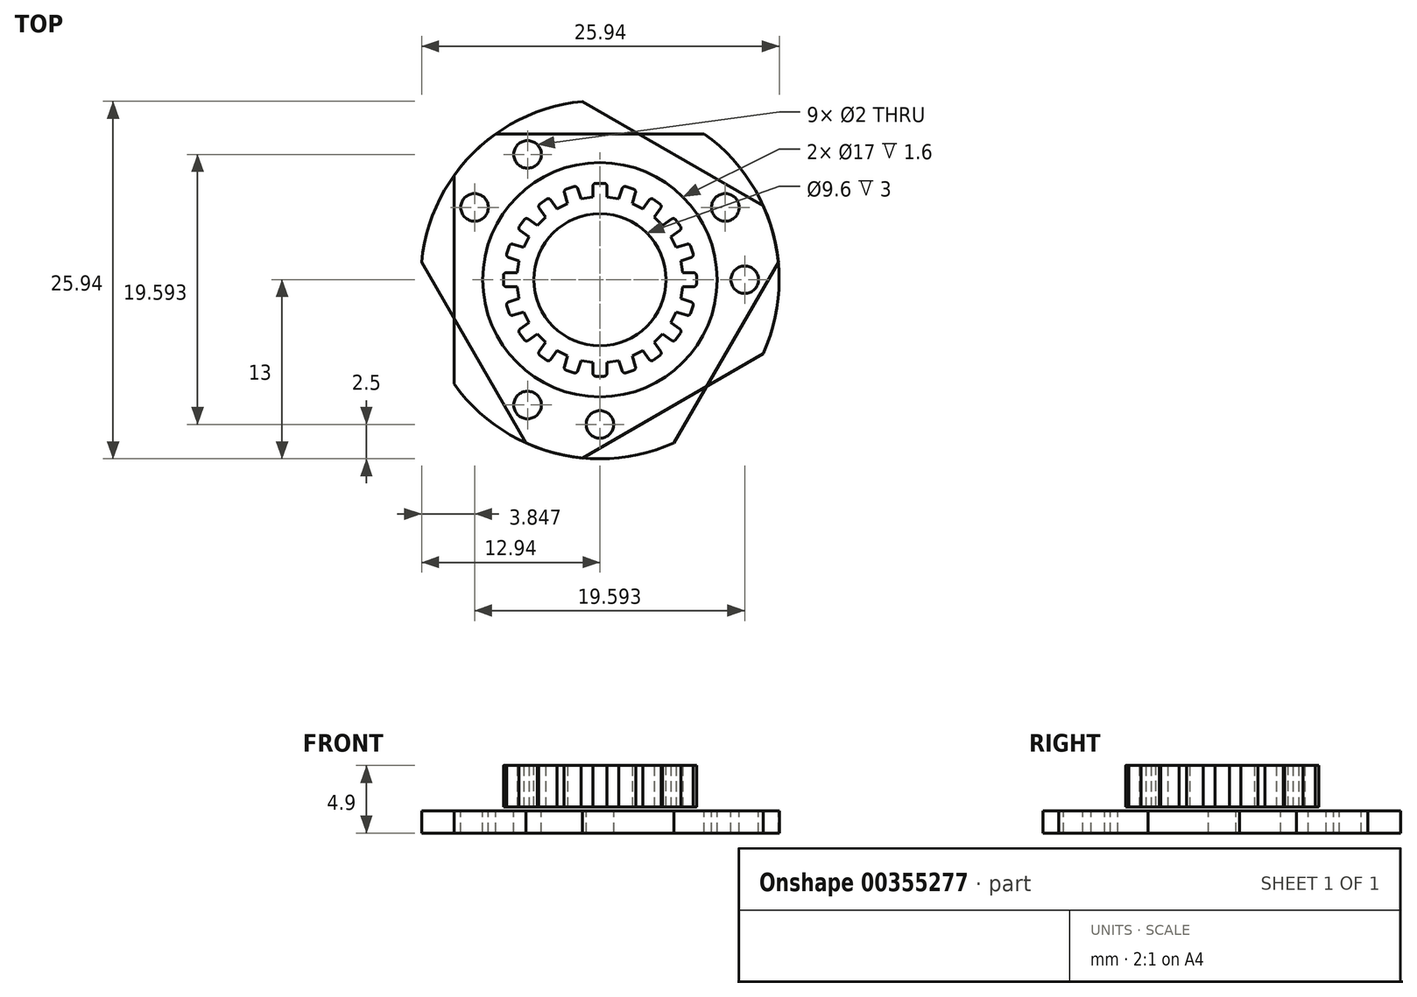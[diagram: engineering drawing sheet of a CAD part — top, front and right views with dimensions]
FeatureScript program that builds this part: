
annotation { "Feature Type Name" : "Feature", "Feature Type Description" : "" }
export const myFeature = defineFeature(function(context is Context, id is Id, definition is map)
    precondition{}
    {
        {
            assignVariable(context, id + "F0", {"name" : "THICK", "anyValue" : 3});
        }
        {
            var Q0;
            Q0=qCreatedBy(makeId("Top.planeOp"),FACE);
            var sketch = newSketch(context, id + "F1", { "sketchPlane" : qUnion([Q0])});
            skCircle(sketch, "E0", {"center": v(0, 0) * mm, "radius": 4 * mm});
            skCircle(sketch, "E1", {"center": v(0, 0) * mm, "radius": 3.5 * mm});
            skCircle(sketch, "E2", {"center": v(0, 0) * mm, "radius": 3 * mm});
            skSolve(sketch);
        }
        {
            var Q0;
            Q0=qCreatedBy(makeId("Top.planeOp"),FACE);
            var sketch = newSketch(context, id + "F2", { "sketchPlane" : qUnion([Q0])});
            skLineSegment(sketch, "E3", {"start": v(0, 0) * mm, "end": v(0, 4.84) * mm, "construction": true});
            skLineSegment(sketch, "E4", {"start": v(1.8, 5.57) * mm, "end": v(0, 0) * mm, "construction": true});
            skLineSegment(sketch, "E5", {"start": v(0.85, 5.38) * mm, "end": v(0, 0) * mm, "construction": true});
            skLineSegment(sketch, "E6", {"start": v(0, 4) * mm, "end": v(0.37, 4) * mm});
            skLineSegment(sketch, "E7", {"start": v(0.52, 3.86) * mm, "end": v(0.58, 2.97) * mm});
            skLineSegment(sketch, "E8", {"start": v(0.58, 2.97) * mm, "end": v(0.93, 2.85) * mm});
            skPoint(sketch, "E9.visualSharp", {"position": v(0.51, 4) * mm});
            skArc(sketch, "E9.filletArc", {"start": v(0.52, 3.86) * mm, "mid": v(0.47, 3.96) * mm, "end": v(0.37, 4) * mm});
            skLineSegment(sketch, "E10.MirrorCS", {"start": v(1.27, 2.74) * mm, "end": v(0.93, 2.85) * mm});
            skLineSegment(sketch, "E11.MirrorCS", {"start": v(2.35, 3.24) * mm, "end": v(2.05, 3.45) * mm});
            skLineSegment(sketch, "E12.MirrorCS", {"start": v(1.85, 3.43) * mm, "end": v(1.27, 2.74) * mm});
            skArc(sketch, "E13.MirrorCS", {"start": v(1.85, 3.43) * mm, "mid": v(1.95, 3.48) * mm, "end": v(2.05, 3.45) * mm});
            skLineSegment(sketch, "E14.1.0", {"start": v(-2.35, 3.24) * mm, "end": v(-2.05, 3.45) * mm});
            skArc(sketch, "E14.1.1", {"start": v(-1.85, 3.43) * mm, "mid": v(-1.95, 3.48) * mm, "end": v(-2.05, 3.45) * mm});
            skLineSegment(sketch, "E14.1.2", {"start": v(-1.85, 3.43) * mm, "end": v(-1.27, 2.74) * mm});
            skLineSegment(sketch, "E14.1.3", {"start": v(-1.27, 2.74) * mm, "end": v(-0.93, 2.85) * mm});
            skLineSegment(sketch, "E14.1.4", {"start": v(-0.58, 2.97) * mm, "end": v(-0.93, 2.85) * mm});
            skLineSegment(sketch, "E14.1.5", {"start": v(-0.52, 3.86) * mm, "end": v(-0.58, 2.97) * mm});
            skLineSegment(sketch, "E14.1.6", {"start": v(0, 4) * mm, "end": v(-0.37, 4) * mm});
            skArc(sketch, "E14.1.7", {"start": v(-0.52, 3.86) * mm, "mid": v(-0.47, 3.96) * mm, "end": v(-0.37, 4) * mm});
            skLineSegment(sketch, "E14.2.0", {"start": v(-3.8, 1.24) * mm, "end": v(-3.69, 1.59) * mm});
            skArc(sketch, "E14.2.1", {"start": v(-3.51, 1.69) * mm, "mid": v(-3.62, 1.67) * mm, "end": v(-3.69, 1.59) * mm});
            skLineSegment(sketch, "E14.2.2", {"start": v(-3.51, 1.69) * mm, "end": v(-2.64, 1.47) * mm});
            skLineSegment(sketch, "E14.2.3", {"start": v(-2.64, 1.47) * mm, "end": v(-2.43, 1.76) * mm});
            skLineSegment(sketch, "E14.2.4", {"start": v(-2.21, 2.06) * mm, "end": v(-2.43, 1.76) * mm});
            skLineSegment(sketch, "E14.2.5", {"start": v(-2.69, 2.82) * mm, "end": v(-2.21, 2.06) * mm});
            skLineSegment(sketch, "E14.2.6", {"start": v(-2.35, 3.24) * mm, "end": v(-2.65, 3.02) * mm});
            skArc(sketch, "E14.2.7", {"start": v(-2.69, 2.82) * mm, "mid": v(-2.7, 2.93) * mm, "end": v(-2.65, 3.02) * mm});
            skLineSegment(sketch, "E14.3.0", {"start": v(-3.8, -1.24) * mm, "end": v(-3.92, -0.88) * mm});
            skArc(sketch, "E14.3.1", {"start": v(-3.83, -0.7) * mm, "mid": v(-3.91, -0.77) * mm, "end": v(-3.92, -0.88) * mm});
            skLineSegment(sketch, "E14.3.2", {"start": v(-3.83, -0.7) * mm, "end": v(-3, -0.37) * mm});
            skLineSegment(sketch, "E14.3.3", {"start": v(-3, -0.37) * mm, "end": v(-3, 0) * mm});
            skLineSegment(sketch, "E14.3.4", {"start": v(-3, 0.37) * mm, "end": v(-3, 0) * mm});
            skLineSegment(sketch, "E14.3.5", {"start": v(-3.83, 0.7) * mm, "end": v(-3, 0.37) * mm});
            skLineSegment(sketch, "E14.3.6", {"start": v(-3.8, 1.24) * mm, "end": v(-3.92, 0.88) * mm});
            skArc(sketch, "E14.3.7", {"start": v(-3.83, 0.7) * mm, "mid": v(-3.91, 0.77) * mm, "end": v(-3.92, 0.88) * mm});
            skLineSegment(sketch, "E14.4.0", {"start": v(-2.35, -3.24) * mm, "end": v(-2.65, -3.02) * mm});
            skArc(sketch, "E14.4.1", {"start": v(-2.69, -2.82) * mm, "mid": v(-2.7, -2.93) * mm, "end": v(-2.65, -3.02) * mm});
            skLineSegment(sketch, "E14.4.2", {"start": v(-2.69, -2.82) * mm, "end": v(-2.21, -2.06) * mm});
            skLineSegment(sketch, "E14.4.3", {"start": v(-2.21, -2.06) * mm, "end": v(-2.43, -1.76) * mm});
            skLineSegment(sketch, "E14.4.4", {"start": v(-2.64, -1.47) * mm, "end": v(-2.43, -1.76) * mm});
            skLineSegment(sketch, "E14.4.5", {"start": v(-3.51, -1.69) * mm, "end": v(-2.64, -1.47) * mm});
            skLineSegment(sketch, "E14.4.6", {"start": v(-3.8, -1.24) * mm, "end": v(-3.69, -1.59) * mm});
            skArc(sketch, "E14.4.7", {"start": v(-3.51, -1.69) * mm, "mid": v(-3.62, -1.67) * mm, "end": v(-3.69, -1.59) * mm});
            skLineSegment(sketch, "E14.5.0", {"start": v(0, -4) * mm, "end": v(-0.37, -4) * mm});
            skArc(sketch, "E14.5.1", {"start": v(-0.52, -3.86) * mm, "mid": v(-0.47, -3.96) * mm, "end": v(-0.37, -4) * mm});
            skLineSegment(sketch, "E14.5.2", {"start": v(-0.52, -3.86) * mm, "end": v(-0.58, -2.97) * mm});
            skLineSegment(sketch, "E14.5.3", {"start": v(-0.58, -2.97) * mm, "end": v(-0.93, -2.85) * mm});
            skLineSegment(sketch, "E14.5.4", {"start": v(-1.27, -2.74) * mm, "end": v(-0.93, -2.85) * mm});
            skLineSegment(sketch, "E14.5.5", {"start": v(-1.85, -3.43) * mm, "end": v(-1.27, -2.74) * mm});
            skLineSegment(sketch, "E14.5.6", {"start": v(-2.35, -3.24) * mm, "end": v(-2.05, -3.45) * mm});
            skArc(sketch, "E14.5.7", {"start": v(-1.85, -3.43) * mm, "mid": v(-1.95, -3.48) * mm, "end": v(-2.05, -3.45) * mm});
            skLineSegment(sketch, "E14.6.0", {"start": v(2.35, -3.24) * mm, "end": v(2.05, -3.45) * mm});
            skArc(sketch, "E14.6.1", {"start": v(1.85, -3.43) * mm, "mid": v(1.95, -3.48) * mm, "end": v(2.05, -3.45) * mm});
            skLineSegment(sketch, "E14.6.2", {"start": v(1.85, -3.43) * mm, "end": v(1.27, -2.74) * mm});
            skLineSegment(sketch, "E14.6.3", {"start": v(1.27, -2.74) * mm, "end": v(0.93, -2.85) * mm});
            skLineSegment(sketch, "E14.6.4", {"start": v(0.58, -2.97) * mm, "end": v(0.93, -2.85) * mm});
            skLineSegment(sketch, "E14.6.5", {"start": v(0.52, -3.86) * mm, "end": v(0.58, -2.97) * mm});
            skLineSegment(sketch, "E14.6.6", {"start": v(0, -4) * mm, "end": v(0.37, -4) * mm});
            skArc(sketch, "E14.6.7", {"start": v(0.52, -3.86) * mm, "mid": v(0.47, -3.96) * mm, "end": v(0.37, -4) * mm});
            skLineSegment(sketch, "E14.7.0", {"start": v(3.8, -1.24) * mm, "end": v(3.69, -1.59) * mm});
            skArc(sketch, "E14.7.1", {"start": v(3.51, -1.69) * mm, "mid": v(3.62, -1.67) * mm, "end": v(3.69, -1.59) * mm});
            skLineSegment(sketch, "E14.7.2", {"start": v(3.51, -1.69) * mm, "end": v(2.64, -1.47) * mm});
            skLineSegment(sketch, "E14.7.3", {"start": v(2.64, -1.47) * mm, "end": v(2.43, -1.76) * mm});
            skLineSegment(sketch, "E14.7.4", {"start": v(2.21, -2.06) * mm, "end": v(2.43, -1.76) * mm});
            skLineSegment(sketch, "E14.7.5", {"start": v(2.69, -2.82) * mm, "end": v(2.21, -2.06) * mm});
            skLineSegment(sketch, "E14.7.6", {"start": v(2.35, -3.24) * mm, "end": v(2.65, -3.02) * mm});
            skArc(sketch, "E14.7.7", {"start": v(2.69, -2.82) * mm, "mid": v(2.7, -2.93) * mm, "end": v(2.65, -3.02) * mm});
            skLineSegment(sketch, "E14.8.0", {"start": v(3.8, 1.24) * mm, "end": v(3.92, 0.88) * mm});
            skArc(sketch, "E14.8.1", {"start": v(3.83, 0.7) * mm, "mid": v(3.91, 0.77) * mm, "end": v(3.92, 0.88) * mm});
            skLineSegment(sketch, "E14.8.2", {"start": v(3.83, 0.7) * mm, "end": v(3, 0.37) * mm});
            skLineSegment(sketch, "E14.8.3", {"start": v(3, 0.37) * mm, "end": v(3, 0) * mm});
            skLineSegment(sketch, "E14.8.4", {"start": v(3, -0.37) * mm, "end": v(3, 0) * mm});
            skLineSegment(sketch, "E14.8.5", {"start": v(3.83, -0.7) * mm, "end": v(3, -0.37) * mm});
            skLineSegment(sketch, "E14.8.6", {"start": v(3.8, -1.24) * mm, "end": v(3.92, -0.88) * mm});
            skArc(sketch, "E14.8.7", {"start": v(3.83, -0.7) * mm, "mid": v(3.91, -0.77) * mm, "end": v(3.92, -0.88) * mm});
            skLineSegment(sketch, "E14.9.0", {"start": v(2.35, 3.24) * mm, "end": v(2.65, 3.02) * mm});
            skArc(sketch, "E14.9.1", {"start": v(2.69, 2.82) * mm, "mid": v(2.7, 2.93) * mm, "end": v(2.65, 3.02) * mm});
            skLineSegment(sketch, "E14.9.2", {"start": v(2.69, 2.82) * mm, "end": v(2.21, 2.06) * mm});
            skLineSegment(sketch, "E14.9.3", {"start": v(2.21, 2.06) * mm, "end": v(2.43, 1.76) * mm});
            skLineSegment(sketch, "E14.9.4", {"start": v(2.64, 1.47) * mm, "end": v(2.43, 1.76) * mm});
            skLineSegment(sketch, "E14.9.5", {"start": v(3.51, 1.69) * mm, "end": v(2.64, 1.47) * mm});
            skLineSegment(sketch, "E14.9.6", {"start": v(3.8, 1.24) * mm, "end": v(3.69, 1.59) * mm});
            skArc(sketch, "E14.9.7", {"start": v(3.51, 1.69) * mm, "mid": v(3.62, 1.67) * mm, "end": v(3.69, 1.59) * mm});
            skPoint(sketch, "E14.center", {"position": v(0, 0) * mm});
            skSolve(sketch);
        }
        {
            var Q0;
            Q0=qSketchRegion(id+"F2",true);
            extrude(context, id + "F3", {"entities" : qUnion([Q0]), "depth" : (getVariable(context, 'THICK')) * mm});
        }
        {
            var Q0;
            Q0=makeQuery(id+"F3.opExtrude","CAP_FACE",FACE,{"disambiguationData":[OSD([sQuery(id+"F2.wireOp",EDGE,"E6"),sQuery(id+"F2.wireOp",EDGE,"E7"),sQuery(id+"F2.wireOp",EDGE,"E8"),sQuery(id+"F2.wireOp",EDGE,"E9.filletArc"),sQuery(id+"F2.wireOp",EDGE,"E10.MirrorCS"),sQuery(id+"F2.wireOp",EDGE,"E11.MirrorCS"),sQuery(id+"F2.wireOp",EDGE,"E12.MirrorCS"),sQuery(id+"F2.wireOp",EDGE,"E13.MirrorCS"),sQuery(id+"F2.wireOp",EDGE,"E14.1.0"),sQuery(id+"F2.wireOp",EDGE,"E14.1.1"),sQuery(id+"F2.wireOp",EDGE,"E14.1.2"),sQuery(id+"F2.wireOp",EDGE,"E14.1.3"),sQuery(id+"F2.wireOp",EDGE,"E14.1.4"),sQuery(id+"F2.wireOp",EDGE,"E14.1.5"),sQuery(id+"F2.wireOp",EDGE,"E14.1.6"),sQuery(id+"F2.wireOp",EDGE,"E14.1.7"),sQuery(id+"F2.wireOp",EDGE,"E14.2.0"),sQuery(id+"F2.wireOp",EDGE,"E14.2.1"),sQuery(id+"F2.wireOp",EDGE,"E14.2.2"),sQuery(id+"F2.wireOp",EDGE,"E14.2.3"),sQuery(id+"F2.wireOp",EDGE,"E14.2.4"),sQuery(id+"F2.wireOp",EDGE,"E14.2.5"),sQuery(id+"F2.wireOp",EDGE,"E14.2.6"),sQuery(id+"F2.wireOp",EDGE,"E14.2.7"),sQuery(id+"F2.wireOp",EDGE,"E14.3.0"),sQuery(id+"F2.wireOp",EDGE,"E14.3.1"),sQuery(id+"F2.wireOp",EDGE,"E14.3.2"),sQuery(id+"F2.wireOp",EDGE,"E14.3.3"),sQuery(id+"F2.wireOp",EDGE,"E14.3.4"),sQuery(id+"F2.wireOp",EDGE,"E14.3.5"),sQuery(id+"F2.wireOp",EDGE,"E14.3.6"),sQuery(id+"F2.wireOp",EDGE,"E14.3.7"),sQuery(id+"F2.wireOp",EDGE,"E14.4.0"),sQuery(id+"F2.wireOp",EDGE,"E14.4.1"),sQuery(id+"F2.wireOp",EDGE,"E14.4.2"),sQuery(id+"F2.wireOp",EDGE,"E14.4.3"),sQuery(id+"F2.wireOp",EDGE,"E14.4.4"),sQuery(id+"F2.wireOp",EDGE,"E14.4.5"),sQuery(id+"F2.wireOp",EDGE,"E14.4.6"),sQuery(id+"F2.wireOp",EDGE,"E14.4.7"),sQuery(id+"F2.wireOp",EDGE,"E14.5.0"),sQuery(id+"F2.wireOp",EDGE,"E14.5.1"),sQuery(id+"F2.wireOp",EDGE,"E14.5.2"),sQuery(id+"F2.wireOp",EDGE,"E14.5.3"),sQuery(id+"F2.wireOp",EDGE,"E14.5.4"),sQuery(id+"F2.wireOp",EDGE,"E14.5.5"),sQuery(id+"F2.wireOp",EDGE,"E14.5.6"),sQuery(id+"F2.wireOp",EDGE,"E14.5.7"),sQuery(id+"F2.wireOp",EDGE,"E14.6.0"),sQuery(id+"F2.wireOp",EDGE,"E14.6.1"),sQuery(id+"F2.wireOp",EDGE,"E14.6.2"),sQuery(id+"F2.wireOp",EDGE,"E14.6.3"),sQuery(id+"F2.wireOp",EDGE,"E14.6.4"),sQuery(id+"F2.wireOp",EDGE,"E14.6.5"),sQuery(id+"F2.wireOp",EDGE,"E14.6.6"),sQuery(id+"F2.wireOp",EDGE,"E14.6.7"),sQuery(id+"F2.wireOp",EDGE,"E14.7.0"),sQuery(id+"F2.wireOp",EDGE,"E14.7.1"),sQuery(id+"F2.wireOp",EDGE,"E14.7.2"),sQuery(id+"F2.wireOp",EDGE,"E14.7.3"),sQuery(id+"F2.wireOp",EDGE,"E14.7.4"),sQuery(id+"F2.wireOp",EDGE,"E14.7.5"),sQuery(id+"F2.wireOp",EDGE,"E14.7.6"),sQuery(id+"F2.wireOp",EDGE,"E14.7.7"),sQuery(id+"F2.wireOp",EDGE,"E14.8.0"),sQuery(id+"F2.wireOp",EDGE,"E14.8.1"),sQuery(id+"F2.wireOp",EDGE,"E14.8.2"),sQuery(id+"F2.wireOp",EDGE,"E14.8.3"),sQuery(id+"F2.wireOp",EDGE,"E14.8.4"),sQuery(id+"F2.wireOp",EDGE,"E14.8.5"),sQuery(id+"F2.wireOp",EDGE,"E14.8.6"),sQuery(id+"F2.wireOp",EDGE,"E14.8.7"),sQuery(id+"F2.wireOp",EDGE,"E14.9.0"),sQuery(id+"F2.wireOp",EDGE,"E14.9.1"),sQuery(id+"F2.wireOp",EDGE,"E14.9.2"),sQuery(id+"F2.wireOp",EDGE,"E14.9.3"),sQuery(id+"F2.wireOp",EDGE,"E14.9.4"),sQuery(id+"F2.wireOp",EDGE,"E14.9.5"),sQuery(id+"F2.wireOp",EDGE,"E14.9.6"),sQuery(id+"F2.wireOp",EDGE,"E14.9.7")])],"isStart":true});
            var sketch = newSketch(context, id + "F4", { "sketchPlane" : qUnion([Q0])});
            skCircle(sketch, "E15", {"center": v(0, 0) * mm, "radius": 2.25 * mm});
            skSolve(sketch);
        }
        {
            var Q0;
            Q0=qSketchRegion(id+"F4",true);
            extrude(context, id + "F5", {"entities" : qUnion([Q0]), "operationType" : NewBodyOperationType.ADD, "depth" : 0.3 * mm});
        }
        {
            var Q0;
            Q0=makeQuery(id+"F3.opExtrude","SWEPT_BODY",BODY,{"disambiguationData":[OSD([sQuery(id+"F2.wireOp",EDGE,"E6"),sQuery(id+"F2.wireOp",EDGE,"E7"),sQuery(id+"F2.wireOp",EDGE,"E8"),sQuery(id+"F2.wireOp",EDGE,"E9.filletArc"),sQuery(id+"F2.wireOp",EDGE,"E10.MirrorCS"),sQuery(id+"F2.wireOp",EDGE,"E11.MirrorCS"),sQuery(id+"F2.wireOp",EDGE,"E12.MirrorCS"),sQuery(id+"F2.wireOp",EDGE,"E13.MirrorCS"),sQuery(id+"F2.wireOp",EDGE,"E14.1.0"),sQuery(id+"F2.wireOp",EDGE,"E14.1.1"),sQuery(id+"F2.wireOp",EDGE,"E14.1.2"),sQuery(id+"F2.wireOp",EDGE,"E14.1.3"),sQuery(id+"F2.wireOp",EDGE,"E14.1.4"),sQuery(id+"F2.wireOp",EDGE,"E14.1.5"),sQuery(id+"F2.wireOp",EDGE,"E14.1.6"),sQuery(id+"F2.wireOp",EDGE,"E14.1.7"),sQuery(id+"F2.wireOp",EDGE,"E14.2.0"),sQuery(id+"F2.wireOp",EDGE,"E14.2.1"),sQuery(id+"F2.wireOp",EDGE,"E14.2.2"),sQuery(id+"F2.wireOp",EDGE,"E14.2.3"),sQuery(id+"F2.wireOp",EDGE,"E14.2.4"),sQuery(id+"F2.wireOp",EDGE,"E14.2.5"),sQuery(id+"F2.wireOp",EDGE,"E14.2.6"),sQuery(id+"F2.wireOp",EDGE,"E14.2.7"),sQuery(id+"F2.wireOp",EDGE,"E14.3.0"),sQuery(id+"F2.wireOp",EDGE,"E14.3.1"),sQuery(id+"F2.wireOp",EDGE,"E14.3.2"),sQuery(id+"F2.wireOp",EDGE,"E14.3.3"),sQuery(id+"F2.wireOp",EDGE,"E14.3.4"),sQuery(id+"F2.wireOp",EDGE,"E14.3.5"),sQuery(id+"F2.wireOp",EDGE,"E14.3.6"),sQuery(id+"F2.wireOp",EDGE,"E14.3.7"),sQuery(id+"F2.wireOp",EDGE,"E14.4.0"),sQuery(id+"F2.wireOp",EDGE,"E14.4.1"),sQuery(id+"F2.wireOp",EDGE,"E14.4.2"),sQuery(id+"F2.wireOp",EDGE,"E14.4.3"),sQuery(id+"F2.wireOp",EDGE,"E14.4.4"),sQuery(id+"F2.wireOp",EDGE,"E14.4.5"),sQuery(id+"F2.wireOp",EDGE,"E14.4.6"),sQuery(id+"F2.wireOp",EDGE,"E14.4.7"),sQuery(id+"F2.wireOp",EDGE,"E14.5.0"),sQuery(id+"F2.wireOp",EDGE,"E14.5.1"),sQuery(id+"F2.wireOp",EDGE,"E14.5.2"),sQuery(id+"F2.wireOp",EDGE,"E14.5.3"),sQuery(id+"F2.wireOp",EDGE,"E14.5.4"),sQuery(id+"F2.wireOp",EDGE,"E14.5.5"),sQuery(id+"F2.wireOp",EDGE,"E14.5.6"),sQuery(id+"F2.wireOp",EDGE,"E14.5.7"),sQuery(id+"F2.wireOp",EDGE,"E14.6.0"),sQuery(id+"F2.wireOp",EDGE,"E14.6.1"),sQuery(id+"F2.wireOp",EDGE,"E14.6.2"),sQuery(id+"F2.wireOp",EDGE,"E14.6.3"),sQuery(id+"F2.wireOp",EDGE,"E14.6.4"),sQuery(id+"F2.wireOp",EDGE,"E14.6.5"),sQuery(id+"F2.wireOp",EDGE,"E14.6.6"),sQuery(id+"F2.wireOp",EDGE,"E14.6.7"),sQuery(id+"F2.wireOp",EDGE,"E14.7.0"),sQuery(id+"F2.wireOp",EDGE,"E14.7.1"),sQuery(id+"F2.wireOp",EDGE,"E14.7.2"),sQuery(id+"F2.wireOp",EDGE,"E14.7.3"),sQuery(id+"F2.wireOp",EDGE,"E14.7.4"),sQuery(id+"F2.wireOp",EDGE,"E14.7.5"),sQuery(id+"F2.wireOp",EDGE,"E14.7.6"),sQuery(id+"F2.wireOp",EDGE,"E14.7.7"),sQuery(id+"F2.wireOp",EDGE,"E14.8.0"),sQuery(id+"F2.wireOp",EDGE,"E14.8.1"),sQuery(id+"F2.wireOp",EDGE,"E14.8.2"),sQuery(id+"F2.wireOp",EDGE,"E14.8.3"),sQuery(id+"F2.wireOp",EDGE,"E14.8.4"),sQuery(id+"F2.wireOp",EDGE,"E14.8.5"),sQuery(id+"F2.wireOp",EDGE,"E14.8.6"),sQuery(id+"F2.wireOp",EDGE,"E14.8.7"),sQuery(id+"F2.wireOp",EDGE,"E14.9.0"),sQuery(id+"F2.wireOp",EDGE,"E14.9.1"),sQuery(id+"F2.wireOp",EDGE,"E14.9.2"),sQuery(id+"F2.wireOp",EDGE,"E14.9.3"),sQuery(id+"F2.wireOp",EDGE,"E14.9.4"),sQuery(id+"F2.wireOp",EDGE,"E14.9.5"),sQuery(id+"F2.wireOp",EDGE,"E14.9.6"),sQuery(id+"F2.wireOp",EDGE,"E14.9.7")])]});
            transform(context, id + "F6", {"entities" : qUnion([Q0]), "transformType" : TransformType.COPY});
        }
        {
            var Q0;
            Q0=makeQuery(id+"F3.opExtrude","CAP_FACE",FACE,{"disambiguationData":[OSD([sQuery(id+"F2.wireOp",EDGE,"E6"),sQuery(id+"F2.wireOp",EDGE,"E7"),sQuery(id+"F2.wireOp",EDGE,"E8"),sQuery(id+"F2.wireOp",EDGE,"E9.filletArc"),sQuery(id+"F2.wireOp",EDGE,"E10.MirrorCS"),sQuery(id+"F2.wireOp",EDGE,"E11.MirrorCS"),sQuery(id+"F2.wireOp",EDGE,"E12.MirrorCS"),sQuery(id+"F2.wireOp",EDGE,"E13.MirrorCS"),sQuery(id+"F2.wireOp",EDGE,"E14.1.0"),sQuery(id+"F2.wireOp",EDGE,"E14.1.1"),sQuery(id+"F2.wireOp",EDGE,"E14.1.2"),sQuery(id+"F2.wireOp",EDGE,"E14.1.3"),sQuery(id+"F2.wireOp",EDGE,"E14.1.4"),sQuery(id+"F2.wireOp",EDGE,"E14.1.5"),sQuery(id+"F2.wireOp",EDGE,"E14.1.6"),sQuery(id+"F2.wireOp",EDGE,"E14.1.7"),sQuery(id+"F2.wireOp",EDGE,"E14.2.0"),sQuery(id+"F2.wireOp",EDGE,"E14.2.1"),sQuery(id+"F2.wireOp",EDGE,"E14.2.2"),sQuery(id+"F2.wireOp",EDGE,"E14.2.3"),sQuery(id+"F2.wireOp",EDGE,"E14.2.4"),sQuery(id+"F2.wireOp",EDGE,"E14.2.5"),sQuery(id+"F2.wireOp",EDGE,"E14.2.6"),sQuery(id+"F2.wireOp",EDGE,"E14.2.7"),sQuery(id+"F2.wireOp",EDGE,"E14.3.0"),sQuery(id+"F2.wireOp",EDGE,"E14.3.1"),sQuery(id+"F2.wireOp",EDGE,"E14.3.2"),sQuery(id+"F2.wireOp",EDGE,"E14.3.3"),sQuery(id+"F2.wireOp",EDGE,"E14.3.4"),sQuery(id+"F2.wireOp",EDGE,"E14.3.5"),sQuery(id+"F2.wireOp",EDGE,"E14.3.6"),sQuery(id+"F2.wireOp",EDGE,"E14.3.7"),sQuery(id+"F2.wireOp",EDGE,"E14.4.0"),sQuery(id+"F2.wireOp",EDGE,"E14.4.1"),sQuery(id+"F2.wireOp",EDGE,"E14.4.2"),sQuery(id+"F2.wireOp",EDGE,"E14.4.3"),sQuery(id+"F2.wireOp",EDGE,"E14.4.4"),sQuery(id+"F2.wireOp",EDGE,"E14.4.5"),sQuery(id+"F2.wireOp",EDGE,"E14.4.6"),sQuery(id+"F2.wireOp",EDGE,"E14.4.7"),sQuery(id+"F2.wireOp",EDGE,"E14.5.0"),sQuery(id+"F2.wireOp",EDGE,"E14.5.1"),sQuery(id+"F2.wireOp",EDGE,"E14.5.2"),sQuery(id+"F2.wireOp",EDGE,"E14.5.3"),sQuery(id+"F2.wireOp",EDGE,"E14.5.4"),sQuery(id+"F2.wireOp",EDGE,"E14.5.5"),sQuery(id+"F2.wireOp",EDGE,"E14.5.6"),sQuery(id+"F2.wireOp",EDGE,"E14.5.7"),sQuery(id+"F2.wireOp",EDGE,"E14.6.0"),sQuery(id+"F2.wireOp",EDGE,"E14.6.1"),sQuery(id+"F2.wireOp",EDGE,"E14.6.2"),sQuery(id+"F2.wireOp",EDGE,"E14.6.3"),sQuery(id+"F2.wireOp",EDGE,"E14.6.4"),sQuery(id+"F2.wireOp",EDGE,"E14.6.5"),sQuery(id+"F2.wireOp",EDGE,"E14.6.6"),sQuery(id+"F2.wireOp",EDGE,"E14.6.7"),sQuery(id+"F2.wireOp",EDGE,"E14.7.0"),sQuery(id+"F2.wireOp",EDGE,"E14.7.1"),sQuery(id+"F2.wireOp",EDGE,"E14.7.2"),sQuery(id+"F2.wireOp",EDGE,"E14.7.3"),sQuery(id+"F2.wireOp",EDGE,"E14.7.4"),sQuery(id+"F2.wireOp",EDGE,"E14.7.5"),sQuery(id+"F2.wireOp",EDGE,"E14.7.6"),sQuery(id+"F2.wireOp",EDGE,"E14.7.7"),sQuery(id+"F2.wireOp",EDGE,"E14.8.0"),sQuery(id+"F2.wireOp",EDGE,"E14.8.1"),sQuery(id+"F2.wireOp",EDGE,"E14.8.2"),sQuery(id+"F2.wireOp",EDGE,"E14.8.3"),sQuery(id+"F2.wireOp",EDGE,"E14.8.4"),sQuery(id+"F2.wireOp",EDGE,"E14.8.5"),sQuery(id+"F2.wireOp",EDGE,"E14.8.6"),sQuery(id+"F2.wireOp",EDGE,"E14.8.7"),sQuery(id+"F2.wireOp",EDGE,"E14.9.0"),sQuery(id+"F2.wireOp",EDGE,"E14.9.1"),sQuery(id+"F2.wireOp",EDGE,"E14.9.2"),sQuery(id+"F2.wireOp",EDGE,"E14.9.3"),sQuery(id+"F2.wireOp",EDGE,"E14.9.4"),sQuery(id+"F2.wireOp",EDGE,"E14.9.5"),sQuery(id+"F2.wireOp",EDGE,"E14.9.6"),sQuery(id+"F2.wireOp",EDGE,"E14.9.7")])],"isStart":false});
            var sketch = newSketch(context, id + "F7", { "sketchPlane" : qUnion([Q0])});
            skCircle(sketch, "E16.cCircle", {"center": v(0, 0) * mm, "radius": 0.86 * mm, "construction": true});
            skLineSegment(sketch, "E16.0", {"start": v(0.86, 0.5) * mm, "end": v(0.86, -0.5) * mm});
            skLineSegment(sketch, "E16.1", {"start": v(0.86, -0.5) * mm, "end": v(0, -1) * mm});
            skLineSegment(sketch, "E16.2", {"start": v(0, -1) * mm, "end": v(-0.86, -0.5) * mm});
            skLineSegment(sketch, "E16.3", {"start": v(-0.86, -0.5) * mm, "end": v(-0.86, 0.5) * mm});
            skLineSegment(sketch, "E16.4", {"start": v(-0.86, 0.5) * mm, "end": v(0, 1) * mm});
            skLineSegment(sketch, "E16.5", {"start": v(0, 1) * mm, "end": v(0.86, 0.5) * mm});
            skPoint(sketch, "E16.0.midPoint", {"position": v(0.86, 0) * mm});
            skSolve(sketch);
        }
        {
            var Q0;
            Q0=qSketchRegion(id+"F7",true);
            extrude(context, id + "F8", {"entities" : qUnion([Q0]), "operationType" : NewBodyOperationType.REMOVE, "oppositeDirection" : true, "depth" : 25 * mm});
        }
        {
            var Q0;
            Q0=makeQuery(id+"F3.opExtrude","CAP_FACE",FACE,{"disambiguationData":[OSD([sQuery(id+"F2.wireOp",EDGE,"E6"),sQuery(id+"F2.wireOp",EDGE,"E7"),sQuery(id+"F2.wireOp",EDGE,"E8"),sQuery(id+"F2.wireOp",EDGE,"E9.filletArc"),sQuery(id+"F2.wireOp",EDGE,"E10.MirrorCS"),sQuery(id+"F2.wireOp",EDGE,"E11.MirrorCS"),sQuery(id+"F2.wireOp",EDGE,"E12.MirrorCS"),sQuery(id+"F2.wireOp",EDGE,"E13.MirrorCS"),sQuery(id+"F2.wireOp",EDGE,"E14.1.0"),sQuery(id+"F2.wireOp",EDGE,"E14.1.1"),sQuery(id+"F2.wireOp",EDGE,"E14.1.2"),sQuery(id+"F2.wireOp",EDGE,"E14.1.3"),sQuery(id+"F2.wireOp",EDGE,"E14.1.4"),sQuery(id+"F2.wireOp",EDGE,"E14.1.5"),sQuery(id+"F2.wireOp",EDGE,"E14.1.6"),sQuery(id+"F2.wireOp",EDGE,"E14.1.7"),sQuery(id+"F2.wireOp",EDGE,"E14.2.0"),sQuery(id+"F2.wireOp",EDGE,"E14.2.1"),sQuery(id+"F2.wireOp",EDGE,"E14.2.2"),sQuery(id+"F2.wireOp",EDGE,"E14.2.3"),sQuery(id+"F2.wireOp",EDGE,"E14.2.4"),sQuery(id+"F2.wireOp",EDGE,"E14.2.5"),sQuery(id+"F2.wireOp",EDGE,"E14.2.6"),sQuery(id+"F2.wireOp",EDGE,"E14.2.7"),sQuery(id+"F2.wireOp",EDGE,"E14.3.0"),sQuery(id+"F2.wireOp",EDGE,"E14.3.1"),sQuery(id+"F2.wireOp",EDGE,"E14.3.2"),sQuery(id+"F2.wireOp",EDGE,"E14.3.3"),sQuery(id+"F2.wireOp",EDGE,"E14.3.4"),sQuery(id+"F2.wireOp",EDGE,"E14.3.5"),sQuery(id+"F2.wireOp",EDGE,"E14.3.6"),sQuery(id+"F2.wireOp",EDGE,"E14.3.7"),sQuery(id+"F2.wireOp",EDGE,"E14.4.0"),sQuery(id+"F2.wireOp",EDGE,"E14.4.1"),sQuery(id+"F2.wireOp",EDGE,"E14.4.2"),sQuery(id+"F2.wireOp",EDGE,"E14.4.3"),sQuery(id+"F2.wireOp",EDGE,"E14.4.4"),sQuery(id+"F2.wireOp",EDGE,"E14.4.5"),sQuery(id+"F2.wireOp",EDGE,"E14.4.6"),sQuery(id+"F2.wireOp",EDGE,"E14.4.7"),sQuery(id+"F2.wireOp",EDGE,"E14.5.0"),sQuery(id+"F2.wireOp",EDGE,"E14.5.1"),sQuery(id+"F2.wireOp",EDGE,"E14.5.2"),sQuery(id+"F2.wireOp",EDGE,"E14.5.3"),sQuery(id+"F2.wireOp",EDGE,"E14.5.4"),sQuery(id+"F2.wireOp",EDGE,"E14.5.5"),sQuery(id+"F2.wireOp",EDGE,"E14.5.6"),sQuery(id+"F2.wireOp",EDGE,"E14.5.7"),sQuery(id+"F2.wireOp",EDGE,"E14.6.0"),sQuery(id+"F2.wireOp",EDGE,"E14.6.1"),sQuery(id+"F2.wireOp",EDGE,"E14.6.2"),sQuery(id+"F2.wireOp",EDGE,"E14.6.3"),sQuery(id+"F2.wireOp",EDGE,"E14.6.4"),sQuery(id+"F2.wireOp",EDGE,"E14.6.5"),sQuery(id+"F2.wireOp",EDGE,"E14.6.6"),sQuery(id+"F2.wireOp",EDGE,"E14.6.7"),sQuery(id+"F2.wireOp",EDGE,"E14.7.0"),sQuery(id+"F2.wireOp",EDGE,"E14.7.1"),sQuery(id+"F2.wireOp",EDGE,"E14.7.2"),sQuery(id+"F2.wireOp",EDGE,"E14.7.3"),sQuery(id+"F2.wireOp",EDGE,"E14.7.4"),sQuery(id+"F2.wireOp",EDGE,"E14.7.5"),sQuery(id+"F2.wireOp",EDGE,"E14.7.6"),sQuery(id+"F2.wireOp",EDGE,"E14.7.7"),sQuery(id+"F2.wireOp",EDGE,"E14.8.0"),sQuery(id+"F2.wireOp",EDGE,"E14.8.1"),sQuery(id+"F2.wireOp",EDGE,"E14.8.2"),sQuery(id+"F2.wireOp",EDGE,"E14.8.3"),sQuery(id+"F2.wireOp",EDGE,"E14.8.4"),sQuery(id+"F2.wireOp",EDGE,"E14.8.5"),sQuery(id+"F2.wireOp",EDGE,"E14.8.6"),sQuery(id+"F2.wireOp",EDGE,"E14.8.7"),sQuery(id+"F2.wireOp",EDGE,"E14.9.0"),sQuery(id+"F2.wireOp",EDGE,"E14.9.1"),sQuery(id+"F2.wireOp",EDGE,"E14.9.2"),sQuery(id+"F2.wireOp",EDGE,"E14.9.3"),sQuery(id+"F2.wireOp",EDGE,"E14.9.4"),sQuery(id+"F2.wireOp",EDGE,"E14.9.5"),sQuery(id+"F2.wireOp",EDGE,"E14.9.6"),sQuery(id+"F2.wireOp",EDGE,"E14.9.7")])],"isStart":false});
            var sketch = newSketch(context, id + "F9", { "sketchPlane" : qUnion([Q0])});
            skCircle(sketch, "E17", {"center": v(0, 0) * mm, "radius": 1 * mm});
            skSolve(sketch);
        }
        {
            var Q0;
            Q0=qSketchRegion(id+"F9",true);
            extrude(context, id + "F10", {"entities" : qUnion([Q0]), "operationType" : NewBodyOperationType.REMOVE, "oppositeDirection" : true, "depth" : 25 * mm});
        }
        {
            var Q0;
            Q0=makeQuery(id+"F6.opPattern","COPY",BODY,{"derivedFrom":makeQuery(id+"F3.opExtrude","SWEPT_BODY",BODY,{"disambiguationData":[OSD([sQuery(id+"F2.wireOp",EDGE,"E6"),sQuery(id+"F2.wireOp",EDGE,"E7"),sQuery(id+"F2.wireOp",EDGE,"E8"),sQuery(id+"F2.wireOp",EDGE,"E9.filletArc"),sQuery(id+"F2.wireOp",EDGE,"E10.MirrorCS"),sQuery(id+"F2.wireOp",EDGE,"E11.MirrorCS"),sQuery(id+"F2.wireOp",EDGE,"E12.MirrorCS"),sQuery(id+"F2.wireOp",EDGE,"E13.MirrorCS"),sQuery(id+"F2.wireOp",EDGE,"E14.1.0"),sQuery(id+"F2.wireOp",EDGE,"E14.1.1"),sQuery(id+"F2.wireOp",EDGE,"E14.1.2"),sQuery(id+"F2.wireOp",EDGE,"E14.1.3"),sQuery(id+"F2.wireOp",EDGE,"E14.1.4"),sQuery(id+"F2.wireOp",EDGE,"E14.1.5"),sQuery(id+"F2.wireOp",EDGE,"E14.1.6"),sQuery(id+"F2.wireOp",EDGE,"E14.1.7"),sQuery(id+"F2.wireOp",EDGE,"E14.2.0"),sQuery(id+"F2.wireOp",EDGE,"E14.2.1"),sQuery(id+"F2.wireOp",EDGE,"E14.2.2"),sQuery(id+"F2.wireOp",EDGE,"E14.2.3"),sQuery(id+"F2.wireOp",EDGE,"E14.2.4"),sQuery(id+"F2.wireOp",EDGE,"E14.2.5"),sQuery(id+"F2.wireOp",EDGE,"E14.2.6"),sQuery(id+"F2.wireOp",EDGE,"E14.2.7"),sQuery(id+"F2.wireOp",EDGE,"E14.3.0"),sQuery(id+"F2.wireOp",EDGE,"E14.3.1"),sQuery(id+"F2.wireOp",EDGE,"E14.3.2"),sQuery(id+"F2.wireOp",EDGE,"E14.3.3"),sQuery(id+"F2.wireOp",EDGE,"E14.3.4"),sQuery(id+"F2.wireOp",EDGE,"E14.3.5"),sQuery(id+"F2.wireOp",EDGE,"E14.3.6"),sQuery(id+"F2.wireOp",EDGE,"E14.3.7"),sQuery(id+"F2.wireOp",EDGE,"E14.4.0"),sQuery(id+"F2.wireOp",EDGE,"E14.4.1"),sQuery(id+"F2.wireOp",EDGE,"E14.4.2"),sQuery(id+"F2.wireOp",EDGE,"E14.4.3"),sQuery(id+"F2.wireOp",EDGE,"E14.4.4"),sQuery(id+"F2.wireOp",EDGE,"E14.4.5"),sQuery(id+"F2.wireOp",EDGE,"E14.4.6"),sQuery(id+"F2.wireOp",EDGE,"E14.4.7"),sQuery(id+"F2.wireOp",EDGE,"E14.5.0"),sQuery(id+"F2.wireOp",EDGE,"E14.5.1"),sQuery(id+"F2.wireOp",EDGE,"E14.5.2"),sQuery(id+"F2.wireOp",EDGE,"E14.5.3"),sQuery(id+"F2.wireOp",EDGE,"E14.5.4"),sQuery(id+"F2.wireOp",EDGE,"E14.5.5"),sQuery(id+"F2.wireOp",EDGE,"E14.5.6"),sQuery(id+"F2.wireOp",EDGE,"E14.5.7"),sQuery(id+"F2.wireOp",EDGE,"E14.6.0"),sQuery(id+"F2.wireOp",EDGE,"E14.6.1"),sQuery(id+"F2.wireOp",EDGE,"E14.6.2"),sQuery(id+"F2.wireOp",EDGE,"E14.6.3"),sQuery(id+"F2.wireOp",EDGE,"E14.6.4"),sQuery(id+"F2.wireOp",EDGE,"E14.6.5"),sQuery(id+"F2.wireOp",EDGE,"E14.6.6"),sQuery(id+"F2.wireOp",EDGE,"E14.6.7"),sQuery(id+"F2.wireOp",EDGE,"E14.7.0"),sQuery(id+"F2.wireOp",EDGE,"E14.7.1"),sQuery(id+"F2.wireOp",EDGE,"E14.7.2"),sQuery(id+"F2.wireOp",EDGE,"E14.7.3"),sQuery(id+"F2.wireOp",EDGE,"E14.7.4"),sQuery(id+"F2.wireOp",EDGE,"E14.7.5"),sQuery(id+"F2.wireOp",EDGE,"E14.7.6"),sQuery(id+"F2.wireOp",EDGE,"E14.7.7"),sQuery(id+"F2.wireOp",EDGE,"E14.8.0"),sQuery(id+"F2.wireOp",EDGE,"E14.8.1"),sQuery(id+"F2.wireOp",EDGE,"E14.8.2"),sQuery(id+"F2.wireOp",EDGE,"E14.8.3"),sQuery(id+"F2.wireOp",EDGE,"E14.8.4"),sQuery(id+"F2.wireOp",EDGE,"E14.8.5"),sQuery(id+"F2.wireOp",EDGE,"E14.8.6"),sQuery(id+"F2.wireOp",EDGE,"E14.8.7"),sQuery(id+"F2.wireOp",EDGE,"E14.9.0"),sQuery(id+"F2.wireOp",EDGE,"E14.9.1"),sQuery(id+"F2.wireOp",EDGE,"E14.9.2"),sQuery(id+"F2.wireOp",EDGE,"E14.9.3"),sQuery(id+"F2.wireOp",EDGE,"E14.9.4"),sQuery(id+"F2.wireOp",EDGE,"E14.9.5"),sQuery(id+"F2.wireOp",EDGE,"E14.9.6"),sQuery(id+"F2.wireOp",EDGE,"E14.9.7")])]}),"instanceName":"1"});
            transform(context, id + "F11", {"entities" : qUnion([Q0]), "transformType" : TransformType.COPY});
        }
        {
            var Q0;
            Q0=qCreatedBy(makeId("Top.planeOp"),FACE);
            var sketch = newSketch(context, id + "F12", { "sketchPlane" : qUnion([Q0])});
            skCircle(sketch, "E18", {"center": v(0, 0) * mm, "radius": 10.5 * mm});
            skCircle(sketch, "E19", {"center": v(0, 0) * mm, "radius": 11 * mm});
            skCircle(sketch, "E20.0", {"center": v(0, 0) * mm, "radius": 11.5 * mm});
            skSolve(sketch);
        }
        {
            var Q0;
            Q0=qCreatedBy(makeId("Top.planeOp"),FACE);
            var sketch = newSketch(context, id + "F13", { "sketchPlane" : qUnion([Q0])});
            skLineSegment(sketch, "E21", {"start": v(0, 0) * mm, "end": v(0, 15.18) * mm, "construction": true});
            skLineSegment(sketch, "E22", {"start": v(1.56, 14.86) * mm, "end": v(0, 0) * mm, "construction": true});
            skLineSegment(sketch, "E23", {"start": v(0, 0) * mm, "end": v(0.84, 15.95) * mm, "construction": true});
            skLineSegment(sketch, "E24", {"start": v(0, 11.5) * mm, "end": v(0.39, 11.5) * mm});
            skLineSegment(sketch, "E25", {"start": v(0.39, 11.5) * mm, "end": v(0.67, 10.58) * mm});
            skLineSegment(sketch, "E26", {"start": v(0.8, 10.47) * mm, "end": v(1.1, 10.44) * mm});
            skPoint(sketch, "E27.visualSharp", {"position": v(0.7, 10.48) * mm});
            skArc(sketch, "E27.filletArc", {"start": v(0.67, 10.58) * mm, "mid": v(0.72, 10.5) * mm, "end": v(0.8, 10.47) * mm});
            skLineSegment(sketch, "E28.MirrorCS", {"start": v(1.4, 10.41) * mm, "end": v(1.1, 10.44) * mm});
            skArc(sketch, "E29.MirrorCS", {"start": v(1.54, 10.49) * mm, "mid": v(1.48, 10.43) * mm, "end": v(1.4, 10.41) * mm});
            skLineSegment(sketch, "E30.MirrorCS", {"start": v(2.4, 11.25) * mm, "end": v(2.01, 11.33) * mm});
            skLineSegment(sketch, "E31.MirrorCS", {"start": v(2.01, 11.33) * mm, "end": v(1.54, 10.49) * mm});
            skLineSegment(sketch, "E32.1.0", {"start": v(-2.4, 11.25) * mm, "end": v(-2.01, 11.33) * mm});
            skLineSegment(sketch, "E32.1.1", {"start": v(-2.01, 11.33) * mm, "end": v(-1.54, 10.49) * mm});
            skArc(sketch, "E32.1.2", {"start": v(-1.54, 10.49) * mm, "mid": v(-1.48, 10.43) * mm, "end": v(-1.4, 10.41) * mm});
            skLineSegment(sketch, "E32.1.3", {"start": v(-1.4, 10.41) * mm, "end": v(-1.1, 10.44) * mm});
            skLineSegment(sketch, "E32.1.4", {"start": v(-0.8, 10.47) * mm, "end": v(-1.1, 10.44) * mm});
            skArc(sketch, "E32.1.5", {"start": v(-0.67, 10.58) * mm, "mid": v(-0.72, 10.5) * mm, "end": v(-0.8, 10.47) * mm});
            skLineSegment(sketch, "E32.1.6", {"start": v(-0.39, 11.5) * mm, "end": v(-0.67, 10.58) * mm});
            skLineSegment(sketch, "E32.1.7", {"start": v(0, 11.5) * mm, "end": v(-0.39, 11.5) * mm});
            skLineSegment(sketch, "E32.2.0", {"start": v(-4.68, 10.5) * mm, "end": v(-4.32, 10.66) * mm});
            skLineSegment(sketch, "E32.2.1", {"start": v(-4.32, 10.66) * mm, "end": v(-3.7, 9.94) * mm});
            skArc(sketch, "E32.2.2", {"start": v(-3.7, 9.94) * mm, "mid": v(-3.62, 9.9) * mm, "end": v(-3.53, 9.9) * mm});
            skLineSegment(sketch, "E32.2.3", {"start": v(-3.53, 9.9) * mm, "end": v(-3.24, 9.99) * mm});
            skLineSegment(sketch, "E32.2.4", {"start": v(-2.96, 10.08) * mm, "end": v(-3.24, 9.99) * mm});
            skArc(sketch, "E32.2.5", {"start": v(-2.86, 10.2) * mm, "mid": v(-2.89, 10.13) * mm, "end": v(-2.96, 10.08) * mm});
            skLineSegment(sketch, "E32.2.6", {"start": v(-2.77, 11.17) * mm, "end": v(-2.86, 10.2) * mm});
            skLineSegment(sketch, "E32.2.7", {"start": v(-2.4, 11.25) * mm, "end": v(-2.77, 11.17) * mm});
            skLineSegment(sketch, "E32.3.0", {"start": v(-6.76, 9.3) * mm, "end": v(-6.45, 9.53) * mm});
            skLineSegment(sketch, "E32.3.1", {"start": v(-6.45, 9.53) * mm, "end": v(-5.68, 8.95) * mm});
            skArc(sketch, "E32.3.2", {"start": v(-5.68, 8.95) * mm, "mid": v(-5.6, 8.92) * mm, "end": v(-5.51, 8.94) * mm});
            skLineSegment(sketch, "E32.3.3", {"start": v(-5.51, 8.94) * mm, "end": v(-5.25, 9.1) * mm});
            skLineSegment(sketch, "E32.3.4", {"start": v(-4.99, 9.24) * mm, "end": v(-5.25, 9.1) * mm});
            skArc(sketch, "E32.3.5", {"start": v(-4.92, 9.4) * mm, "mid": v(-4.93, 9.3) * mm, "end": v(-4.99, 9.24) * mm});
            skLineSegment(sketch, "E32.3.6", {"start": v(-5.03, 10.35) * mm, "end": v(-4.92, 9.4) * mm});
            skLineSegment(sketch, "E32.3.7", {"start": v(-4.68, 10.5) * mm, "end": v(-5.03, 10.35) * mm});
            skLineSegment(sketch, "E32.4.0", {"start": v(-8.55, 7.7) * mm, "end": v(-8.29, 7.98) * mm});
            skLineSegment(sketch, "E32.4.1", {"start": v(-8.29, 7.98) * mm, "end": v(-7.41, 7.58) * mm});
            skArc(sketch, "E32.4.2", {"start": v(-7.41, 7.58) * mm, "mid": v(-7.33, 7.56) * mm, "end": v(-7.25, 7.6) * mm});
            skLineSegment(sketch, "E32.4.3", {"start": v(-7.25, 7.6) * mm, "end": v(-7.03, 7.8) * mm});
            skLineSegment(sketch, "E32.4.4", {"start": v(-6.8, 8) * mm, "end": v(-7.03, 7.8) * mm});
            skArc(sketch, "E32.4.5", {"start": v(-6.76, 8.16) * mm, "mid": v(-6.76, 8.08) * mm, "end": v(-6.8, 8) * mm});
            skLineSegment(sketch, "E32.4.6", {"start": v(-7.07, 9.08) * mm, "end": v(-6.76, 8.16) * mm});
            skLineSegment(sketch, "E32.4.7", {"start": v(-6.76, 9.3) * mm, "end": v(-7.07, 9.08) * mm});
            skLineSegment(sketch, "E32.5.0", {"start": v(-9.96, 5.75) * mm, "end": v(-9.77, 6.08) * mm});
            skLineSegment(sketch, "E32.5.1", {"start": v(-9.77, 6.08) * mm, "end": v(-8.83, 5.87) * mm});
            skArc(sketch, "E32.5.2", {"start": v(-8.83, 5.87) * mm, "mid": v(-8.74, 5.88) * mm, "end": v(-8.67, 5.93) * mm});
            skLineSegment(sketch, "E32.5.3", {"start": v(-8.67, 5.93) * mm, "end": v(-8.5, 6.17) * mm});
            skLineSegment(sketch, "E32.5.4", {"start": v(-8.32, 6.42) * mm, "end": v(-8.5, 6.17) * mm});
            skArc(sketch, "E32.5.5", {"start": v(-8.31, 6.58) * mm, "mid": v(-8.29, 6.5) * mm, "end": v(-8.32, 6.42) * mm});
            skLineSegment(sketch, "E32.5.6", {"start": v(-8.8, 7.4) * mm, "end": v(-8.31, 6.58) * mm});
            skLineSegment(sketch, "E32.5.7", {"start": v(-8.55, 7.7) * mm, "end": v(-8.8, 7.4) * mm});
            skLineSegment(sketch, "E32.6.0", {"start": v(-10.94, 3.55) * mm, "end": v(-10.82, 3.92) * mm});
            skLineSegment(sketch, "E32.6.1", {"start": v(-10.82, 3.92) * mm, "end": v(-9.85, 3.9) * mm});
            skArc(sketch, "E32.6.2", {"start": v(-9.85, 3.9) * mm, "mid": v(-9.77, 3.93) * mm, "end": v(-9.71, 4) * mm});
            skLineSegment(sketch, "E32.6.3", {"start": v(-9.71, 4) * mm, "end": v(-9.6, 4.27) * mm});
            skLineSegment(sketch, "E32.6.4", {"start": v(-9.47, 4.55) * mm, "end": v(-9.6, 4.27) * mm});
            skArc(sketch, "E32.6.5", {"start": v(-9.5, 4.7) * mm, "mid": v(-9.46, 4.63) * mm, "end": v(-9.47, 4.55) * mm});
            skLineSegment(sketch, "E32.6.6", {"start": v(-10.15, 5.42) * mm, "end": v(-9.5, 4.7) * mm});
            skLineSegment(sketch, "E32.6.7", {"start": v(-9.96, 5.75) * mm, "end": v(-10.15, 5.42) * mm});
            skLineSegment(sketch, "E32.7.0", {"start": v(-11.44, 1.2) * mm, "end": v(-11.4, 1.59) * mm});
            skLineSegment(sketch, "E32.7.1", {"start": v(-11.4, 1.59) * mm, "end": v(-10.45, 1.77) * mm});
            skArc(sketch, "E32.7.2", {"start": v(-10.45, 1.77) * mm, "mid": v(-10.37, 1.81) * mm, "end": v(-10.33, 1.89) * mm});
            skLineSegment(sketch, "E32.7.3", {"start": v(-10.33, 1.89) * mm, "end": v(-10.27, 2.18) * mm});
            skLineSegment(sketch, "E32.7.4", {"start": v(-10.2, 2.48) * mm, "end": v(-10.27, 2.18) * mm});
            skArc(sketch, "E32.7.5", {"start": v(-10.27, 2.63) * mm, "mid": v(-10.22, 2.56) * mm, "end": v(-10.2, 2.48) * mm});
            skLineSegment(sketch, "E32.7.6", {"start": v(-11.06, 3.19) * mm, "end": v(-10.27, 2.63) * mm});
            skLineSegment(sketch, "E32.7.7", {"start": v(-10.94, 3.55) * mm, "end": v(-11.06, 3.19) * mm});
            skLineSegment(sketch, "E32.8.0", {"start": v(-11.44, -1.2) * mm, "end": v(-11.48, -0.82) * mm});
            skLineSegment(sketch, "E32.8.1", {"start": v(-11.48, -0.82) * mm, "end": v(-10.6, -0.44) * mm});
            skArc(sketch, "E32.8.2", {"start": v(-10.6, -0.44) * mm, "mid": v(-10.52, -0.38) * mm, "end": v(-10.5, -0.3) * mm});
            skLineSegment(sketch, "E32.8.3", {"start": v(-10.5, -0.3) * mm, "end": v(-10.5, 0) * mm});
            skLineSegment(sketch, "E32.8.4", {"start": v(-10.5, 0.3) * mm, "end": v(-10.5, 0) * mm});
            skArc(sketch, "E32.8.5", {"start": v(-10.6, 0.44) * mm, "mid": v(-10.52, 0.38) * mm, "end": v(-10.5, 0.3) * mm});
            skLineSegment(sketch, "E32.8.6", {"start": v(-11.48, 0.82) * mm, "end": v(-10.6, 0.44) * mm});
            skLineSegment(sketch, "E32.8.7", {"start": v(-11.44, 1.2) * mm, "end": v(-11.48, 0.82) * mm});
            skLineSegment(sketch, "E32.9.0", {"start": v(-10.94, -3.55) * mm, "end": v(-11.06, -3.19) * mm});
            skLineSegment(sketch, "E32.9.1", {"start": v(-11.06, -3.19) * mm, "end": v(-10.27, -2.63) * mm});
            skArc(sketch, "E32.9.2", {"start": v(-10.27, -2.63) * mm, "mid": v(-10.22, -2.56) * mm, "end": v(-10.2, -2.48) * mm});
            skLineSegment(sketch, "E32.9.3", {"start": v(-10.2, -2.48) * mm, "end": v(-10.27, -2.18) * mm});
            skLineSegment(sketch, "E32.9.4", {"start": v(-10.33, -1.89) * mm, "end": v(-10.27, -2.18) * mm});
            skArc(sketch, "E32.9.5", {"start": v(-10.45, -1.77) * mm, "mid": v(-10.37, -1.81) * mm, "end": v(-10.33, -1.89) * mm});
            skLineSegment(sketch, "E32.9.6", {"start": v(-11.4, -1.59) * mm, "end": v(-10.45, -1.77) * mm});
            skLineSegment(sketch, "E32.9.7", {"start": v(-11.44, -1.2) * mm, "end": v(-11.4, -1.59) * mm});
            skLineSegment(sketch, "E32.10.0", {"start": v(-9.96, -5.75) * mm, "end": v(-10.15, -5.42) * mm});
            skLineSegment(sketch, "E32.10.1", {"start": v(-10.15, -5.42) * mm, "end": v(-9.5, -4.7) * mm});
            skArc(sketch, "E32.10.2", {"start": v(-9.5, -4.7) * mm, "mid": v(-9.46, -4.63) * mm, "end": v(-9.47, -4.55) * mm});
            skLineSegment(sketch, "E32.10.3", {"start": v(-9.47, -4.55) * mm, "end": v(-9.6, -4.27) * mm});
            skLineSegment(sketch, "E32.10.4", {"start": v(-9.71, -4) * mm, "end": v(-9.6, -4.27) * mm});
            skArc(sketch, "E32.10.5", {"start": v(-9.85, -3.9) * mm, "mid": v(-9.77, -3.93) * mm, "end": v(-9.71, -4) * mm});
            skLineSegment(sketch, "E32.10.6", {"start": v(-10.82, -3.92) * mm, "end": v(-9.85, -3.9) * mm});
            skLineSegment(sketch, "E32.10.7", {"start": v(-10.94, -3.55) * mm, "end": v(-10.82, -3.92) * mm});
            skLineSegment(sketch, "E32.11.0", {"start": v(-8.55, -7.7) * mm, "end": v(-8.8, -7.4) * mm});
            skLineSegment(sketch, "E32.11.1", {"start": v(-8.8, -7.4) * mm, "end": v(-8.31, -6.58) * mm});
            skArc(sketch, "E32.11.2", {"start": v(-8.31, -6.58) * mm, "mid": v(-8.29, -6.5) * mm, "end": v(-8.32, -6.42) * mm});
            skLineSegment(sketch, "E32.11.3", {"start": v(-8.32, -6.42) * mm, "end": v(-8.5, -6.17) * mm});
            skLineSegment(sketch, "E32.11.4", {"start": v(-8.67, -5.93) * mm, "end": v(-8.5, -6.17) * mm});
            skArc(sketch, "E32.11.5", {"start": v(-8.83, -5.87) * mm, "mid": v(-8.74, -5.88) * mm, "end": v(-8.67, -5.93) * mm});
            skLineSegment(sketch, "E32.11.6", {"start": v(-9.77, -6.08) * mm, "end": v(-8.83, -5.87) * mm});
            skLineSegment(sketch, "E32.11.7", {"start": v(-9.96, -5.75) * mm, "end": v(-9.77, -6.08) * mm});
            skLineSegment(sketch, "E32.12.0", {"start": v(-6.76, -9.3) * mm, "end": v(-7.07, -9.08) * mm});
            skLineSegment(sketch, "E32.12.1", {"start": v(-7.07, -9.08) * mm, "end": v(-6.76, -8.16) * mm});
            skArc(sketch, "E32.12.2", {"start": v(-6.76, -8.16) * mm, "mid": v(-6.76, -8.08) * mm, "end": v(-6.8, -8) * mm});
            skLineSegment(sketch, "E32.12.3", {"start": v(-6.8, -8) * mm, "end": v(-7.03, -7.8) * mm});
            skLineSegment(sketch, "E32.12.4", {"start": v(-7.25, -7.6) * mm, "end": v(-7.03, -7.8) * mm});
            skArc(sketch, "E32.12.5", {"start": v(-7.41, -7.58) * mm, "mid": v(-7.33, -7.56) * mm, "end": v(-7.25, -7.6) * mm});
            skLineSegment(sketch, "E32.12.6", {"start": v(-8.29, -7.98) * mm, "end": v(-7.41, -7.58) * mm});
            skLineSegment(sketch, "E32.12.7", {"start": v(-8.55, -7.7) * mm, "end": v(-8.29, -7.98) * mm});
            skLineSegment(sketch, "E32.13.0", {"start": v(-4.68, -10.5) * mm, "end": v(-5.03, -10.35) * mm});
            skLineSegment(sketch, "E32.13.1", {"start": v(-5.03, -10.35) * mm, "end": v(-4.92, -9.4) * mm});
            skArc(sketch, "E32.13.2", {"start": v(-4.92, -9.4) * mm, "mid": v(-4.93, -9.3) * mm, "end": v(-4.99, -9.24) * mm});
            skLineSegment(sketch, "E32.13.3", {"start": v(-4.99, -9.24) * mm, "end": v(-5.25, -9.1) * mm});
            skLineSegment(sketch, "E32.13.4", {"start": v(-5.51, -8.94) * mm, "end": v(-5.25, -9.1) * mm});
            skArc(sketch, "E32.13.5", {"start": v(-5.68, -8.95) * mm, "mid": v(-5.6, -8.92) * mm, "end": v(-5.51, -8.94) * mm});
            skLineSegment(sketch, "E32.13.6", {"start": v(-6.45, -9.53) * mm, "end": v(-5.68, -8.95) * mm});
            skLineSegment(sketch, "E32.13.7", {"start": v(-6.76, -9.3) * mm, "end": v(-6.45, -9.53) * mm});
            skLineSegment(sketch, "E32.14.0", {"start": v(-2.4, -11.25) * mm, "end": v(-2.77, -11.17) * mm});
            skLineSegment(sketch, "E32.14.1", {"start": v(-2.77, -11.17) * mm, "end": v(-2.86, -10.2) * mm});
            skArc(sketch, "E32.14.2", {"start": v(-2.86, -10.2) * mm, "mid": v(-2.89, -10.13) * mm, "end": v(-2.96, -10.08) * mm});
            skLineSegment(sketch, "E32.14.3", {"start": v(-2.96, -10.08) * mm, "end": v(-3.24, -9.99) * mm});
            skLineSegment(sketch, "E32.14.4", {"start": v(-3.53, -9.9) * mm, "end": v(-3.24, -9.99) * mm});
            skArc(sketch, "E32.14.5", {"start": v(-3.7, -9.94) * mm, "mid": v(-3.62, -9.9) * mm, "end": v(-3.53, -9.9) * mm});
            skLineSegment(sketch, "E32.14.6", {"start": v(-4.32, -10.66) * mm, "end": v(-3.7, -9.94) * mm});
            skLineSegment(sketch, "E32.14.7", {"start": v(-4.68, -10.5) * mm, "end": v(-4.32, -10.66) * mm});
            skLineSegment(sketch, "E32.15.0", {"start": v(0, -11.5) * mm, "end": v(-0.39, -11.5) * mm});
            skLineSegment(sketch, "E32.15.1", {"start": v(-0.39, -11.5) * mm, "end": v(-0.67, -10.58) * mm});
            skArc(sketch, "E32.15.2", {"start": v(-0.67, -10.58) * mm, "mid": v(-0.72, -10.5) * mm, "end": v(-0.8, -10.47) * mm});
            skLineSegment(sketch, "E32.15.3", {"start": v(-0.8, -10.47) * mm, "end": v(-1.1, -10.44) * mm});
            skLineSegment(sketch, "E32.15.4", {"start": v(-1.4, -10.41) * mm, "end": v(-1.1, -10.44) * mm});
            skArc(sketch, "E32.15.5", {"start": v(-1.54, -10.49) * mm, "mid": v(-1.48, -10.43) * mm, "end": v(-1.4, -10.41) * mm});
            skLineSegment(sketch, "E32.15.6", {"start": v(-2.01, -11.33) * mm, "end": v(-1.54, -10.49) * mm});
            skLineSegment(sketch, "E32.15.7", {"start": v(-2.4, -11.25) * mm, "end": v(-2.01, -11.33) * mm});
            skLineSegment(sketch, "E32.16.0", {"start": v(2.4, -11.25) * mm, "end": v(2.01, -11.33) * mm});
            skLineSegment(sketch, "E32.16.1", {"start": v(2.01, -11.33) * mm, "end": v(1.54, -10.49) * mm});
            skArc(sketch, "E32.16.2", {"start": v(1.54, -10.49) * mm, "mid": v(1.48, -10.43) * mm, "end": v(1.4, -10.41) * mm});
            skLineSegment(sketch, "E32.16.3", {"start": v(1.4, -10.41) * mm, "end": v(1.1, -10.44) * mm});
            skLineSegment(sketch, "E32.16.4", {"start": v(0.8, -10.47) * mm, "end": v(1.1, -10.44) * mm});
            skArc(sketch, "E32.16.5", {"start": v(0.67, -10.58) * mm, "mid": v(0.72, -10.5) * mm, "end": v(0.8, -10.47) * mm});
            skLineSegment(sketch, "E32.16.6", {"start": v(0.39, -11.5) * mm, "end": v(0.67, -10.58) * mm});
            skLineSegment(sketch, "E32.16.7", {"start": v(0, -11.5) * mm, "end": v(0.39, -11.5) * mm});
            skLineSegment(sketch, "E32.17.0", {"start": v(4.68, -10.5) * mm, "end": v(4.32, -10.66) * mm});
            skLineSegment(sketch, "E32.17.1", {"start": v(4.32, -10.66) * mm, "end": v(3.7, -9.94) * mm});
            skArc(sketch, "E32.17.2", {"start": v(3.7, -9.94) * mm, "mid": v(3.62, -9.9) * mm, "end": v(3.53, -9.9) * mm});
            skLineSegment(sketch, "E32.17.3", {"start": v(3.53, -9.9) * mm, "end": v(3.24, -9.99) * mm});
            skLineSegment(sketch, "E32.17.4", {"start": v(2.96, -10.08) * mm, "end": v(3.24, -9.99) * mm});
            skArc(sketch, "E32.17.5", {"start": v(2.86, -10.2) * mm, "mid": v(2.89, -10.13) * mm, "end": v(2.96, -10.08) * mm});
            skLineSegment(sketch, "E32.17.6", {"start": v(2.77, -11.17) * mm, "end": v(2.86, -10.2) * mm});
            skLineSegment(sketch, "E32.17.7", {"start": v(2.4, -11.25) * mm, "end": v(2.77, -11.17) * mm});
            skLineSegment(sketch, "E32.18.0", {"start": v(6.76, -9.3) * mm, "end": v(6.45, -9.53) * mm});
            skLineSegment(sketch, "E32.18.1", {"start": v(6.45, -9.53) * mm, "end": v(5.68, -8.95) * mm});
            skArc(sketch, "E32.18.2", {"start": v(5.68, -8.95) * mm, "mid": v(5.6, -8.92) * mm, "end": v(5.51, -8.94) * mm});
            skLineSegment(sketch, "E32.18.3", {"start": v(5.51, -8.94) * mm, "end": v(5.25, -9.1) * mm});
            skLineSegment(sketch, "E32.18.4", {"start": v(4.99, -9.24) * mm, "end": v(5.25, -9.1) * mm});
            skArc(sketch, "E32.18.5", {"start": v(4.92, -9.4) * mm, "mid": v(4.93, -9.3) * mm, "end": v(4.99, -9.24) * mm});
            skLineSegment(sketch, "E32.18.6", {"start": v(5.03, -10.35) * mm, "end": v(4.92, -9.4) * mm});
            skLineSegment(sketch, "E32.18.7", {"start": v(4.68, -10.5) * mm, "end": v(5.03, -10.35) * mm});
            skLineSegment(sketch, "E32.19.0", {"start": v(8.55, -7.7) * mm, "end": v(8.29, -7.98) * mm});
            skLineSegment(sketch, "E32.19.1", {"start": v(8.29, -7.98) * mm, "end": v(7.41, -7.58) * mm});
            skArc(sketch, "E32.19.2", {"start": v(7.41, -7.58) * mm, "mid": v(7.33, -7.56) * mm, "end": v(7.25, -7.6) * mm});
            skLineSegment(sketch, "E32.19.3", {"start": v(7.25, -7.6) * mm, "end": v(7.03, -7.8) * mm});
            skLineSegment(sketch, "E32.19.4", {"start": v(6.8, -8) * mm, "end": v(7.03, -7.8) * mm});
            skArc(sketch, "E32.19.5", {"start": v(6.76, -8.16) * mm, "mid": v(6.76, -8.08) * mm, "end": v(6.8, -8) * mm});
            skLineSegment(sketch, "E32.19.6", {"start": v(7.07, -9.08) * mm, "end": v(6.76, -8.16) * mm});
            skLineSegment(sketch, "E32.19.7", {"start": v(6.76, -9.3) * mm, "end": v(7.07, -9.08) * mm});
            skLineSegment(sketch, "E32.20.0", {"start": v(9.96, -5.75) * mm, "end": v(9.77, -6.08) * mm});
            skLineSegment(sketch, "E32.20.1", {"start": v(9.77, -6.08) * mm, "end": v(8.83, -5.87) * mm});
            skArc(sketch, "E32.20.2", {"start": v(8.83, -5.87) * mm, "mid": v(8.74, -5.88) * mm, "end": v(8.67, -5.93) * mm});
            skLineSegment(sketch, "E32.20.3", {"start": v(8.67, -5.93) * mm, "end": v(8.5, -6.17) * mm});
            skLineSegment(sketch, "E32.20.4", {"start": v(8.32, -6.42) * mm, "end": v(8.5, -6.17) * mm});
            skArc(sketch, "E32.20.5", {"start": v(8.31, -6.58) * mm, "mid": v(8.29, -6.5) * mm, "end": v(8.32, -6.42) * mm});
            skLineSegment(sketch, "E32.20.6", {"start": v(8.8, -7.4) * mm, "end": v(8.31, -6.58) * mm});
            skLineSegment(sketch, "E32.20.7", {"start": v(8.55, -7.7) * mm, "end": v(8.8, -7.4) * mm});
            skLineSegment(sketch, "E32.21.0", {"start": v(10.94, -3.55) * mm, "end": v(10.82, -3.92) * mm});
            skLineSegment(sketch, "E32.21.1", {"start": v(10.82, -3.92) * mm, "end": v(9.85, -3.9) * mm});
            skArc(sketch, "E32.21.2", {"start": v(9.85, -3.9) * mm, "mid": v(9.77, -3.93) * mm, "end": v(9.71, -4) * mm});
            skLineSegment(sketch, "E32.21.3", {"start": v(9.71, -4) * mm, "end": v(9.6, -4.27) * mm});
            skLineSegment(sketch, "E32.21.4", {"start": v(9.47, -4.55) * mm, "end": v(9.6, -4.27) * mm});
            skArc(sketch, "E32.21.5", {"start": v(9.5, -4.7) * mm, "mid": v(9.46, -4.63) * mm, "end": v(9.47, -4.55) * mm});
            skLineSegment(sketch, "E32.21.6", {"start": v(10.15, -5.42) * mm, "end": v(9.5, -4.7) * mm});
            skLineSegment(sketch, "E32.21.7", {"start": v(9.96, -5.75) * mm, "end": v(10.15, -5.42) * mm});
            skLineSegment(sketch, "E32.22.0", {"start": v(11.44, -1.2) * mm, "end": v(11.4, -1.59) * mm});
            skLineSegment(sketch, "E32.22.1", {"start": v(11.4, -1.59) * mm, "end": v(10.45, -1.77) * mm});
            skArc(sketch, "E32.22.2", {"start": v(10.45, -1.77) * mm, "mid": v(10.37, -1.81) * mm, "end": v(10.33, -1.89) * mm});
            skLineSegment(sketch, "E32.22.3", {"start": v(10.33, -1.89) * mm, "end": v(10.27, -2.18) * mm});
            skLineSegment(sketch, "E32.22.4", {"start": v(10.2, -2.48) * mm, "end": v(10.27, -2.18) * mm});
            skArc(sketch, "E32.22.5", {"start": v(10.27, -2.63) * mm, "mid": v(10.22, -2.56) * mm, "end": v(10.2, -2.48) * mm});
            skLineSegment(sketch, "E32.22.6", {"start": v(11.06, -3.19) * mm, "end": v(10.27, -2.63) * mm});
            skLineSegment(sketch, "E32.22.7", {"start": v(10.94, -3.55) * mm, "end": v(11.06, -3.19) * mm});
            skLineSegment(sketch, "E32.23.0", {"start": v(11.44, 1.2) * mm, "end": v(11.48, 0.82) * mm});
            skLineSegment(sketch, "E32.23.1", {"start": v(11.48, 0.82) * mm, "end": v(10.6, 0.44) * mm});
            skArc(sketch, "E32.23.2", {"start": v(10.6, 0.44) * mm, "mid": v(10.52, 0.38) * mm, "end": v(10.5, 0.3) * mm});
            skLineSegment(sketch, "E32.23.3", {"start": v(10.5, 0.3) * mm, "end": v(10.5, 0) * mm});
            skLineSegment(sketch, "E32.23.4", {"start": v(10.5, -0.3) * mm, "end": v(10.5, 0) * mm});
            skArc(sketch, "E32.23.5", {"start": v(10.6, -0.44) * mm, "mid": v(10.52, -0.38) * mm, "end": v(10.5, -0.3) * mm});
            skLineSegment(sketch, "E32.23.6", {"start": v(11.48, -0.82) * mm, "end": v(10.6, -0.44) * mm});
            skLineSegment(sketch, "E32.23.7", {"start": v(11.44, -1.2) * mm, "end": v(11.48, -0.82) * mm});
            skLineSegment(sketch, "E32.24.0", {"start": v(10.94, 3.55) * mm, "end": v(11.06, 3.19) * mm});
            skLineSegment(sketch, "E32.24.1", {"start": v(11.06, 3.19) * mm, "end": v(10.27, 2.63) * mm});
            skArc(sketch, "E32.24.2", {"start": v(10.27, 2.63) * mm, "mid": v(10.22, 2.56) * mm, "end": v(10.2, 2.48) * mm});
            skLineSegment(sketch, "E32.24.3", {"start": v(10.2, 2.48) * mm, "end": v(10.27, 2.18) * mm});
            skLineSegment(sketch, "E32.24.4", {"start": v(10.33, 1.89) * mm, "end": v(10.27, 2.18) * mm});
            skArc(sketch, "E32.24.5", {"start": v(10.45, 1.77) * mm, "mid": v(10.37, 1.81) * mm, "end": v(10.33, 1.89) * mm});
            skLineSegment(sketch, "E32.24.6", {"start": v(11.4, 1.59) * mm, "end": v(10.45, 1.77) * mm});
            skLineSegment(sketch, "E32.24.7", {"start": v(11.44, 1.2) * mm, "end": v(11.4, 1.59) * mm});
            skLineSegment(sketch, "E32.25.0", {"start": v(9.96, 5.75) * mm, "end": v(10.15, 5.42) * mm});
            skLineSegment(sketch, "E32.25.1", {"start": v(10.15, 5.42) * mm, "end": v(9.5, 4.7) * mm});
            skArc(sketch, "E32.25.2", {"start": v(9.5, 4.7) * mm, "mid": v(9.46, 4.63) * mm, "end": v(9.47, 4.55) * mm});
            skLineSegment(sketch, "E32.25.3", {"start": v(9.47, 4.55) * mm, "end": v(9.6, 4.27) * mm});
            skLineSegment(sketch, "E32.25.4", {"start": v(9.71, 4) * mm, "end": v(9.6, 4.27) * mm});
            skArc(sketch, "E32.25.5", {"start": v(9.85, 3.9) * mm, "mid": v(9.77, 3.93) * mm, "end": v(9.71, 4) * mm});
            skLineSegment(sketch, "E32.25.6", {"start": v(10.82, 3.92) * mm, "end": v(9.85, 3.9) * mm});
            skLineSegment(sketch, "E32.25.7", {"start": v(10.94, 3.55) * mm, "end": v(10.82, 3.92) * mm});
            skLineSegment(sketch, "E32.26.0", {"start": v(8.55, 7.7) * mm, "end": v(8.8, 7.4) * mm});
            skLineSegment(sketch, "E32.26.1", {"start": v(8.8, 7.4) * mm, "end": v(8.31, 6.58) * mm});
            skArc(sketch, "E32.26.2", {"start": v(8.31, 6.58) * mm, "mid": v(8.29, 6.5) * mm, "end": v(8.32, 6.42) * mm});
            skLineSegment(sketch, "E32.26.3", {"start": v(8.32, 6.42) * mm, "end": v(8.5, 6.17) * mm});
            skLineSegment(sketch, "E32.26.4", {"start": v(8.67, 5.93) * mm, "end": v(8.5, 6.17) * mm});
            skArc(sketch, "E32.26.5", {"start": v(8.83, 5.87) * mm, "mid": v(8.74, 5.88) * mm, "end": v(8.67, 5.93) * mm});
            skLineSegment(sketch, "E32.26.6", {"start": v(9.77, 6.08) * mm, "end": v(8.83, 5.87) * mm});
            skLineSegment(sketch, "E32.26.7", {"start": v(9.96, 5.75) * mm, "end": v(9.77, 6.08) * mm});
            skLineSegment(sketch, "E32.27.0", {"start": v(6.76, 9.3) * mm, "end": v(7.07, 9.08) * mm});
            skLineSegment(sketch, "E32.27.1", {"start": v(7.07, 9.08) * mm, "end": v(6.76, 8.16) * mm});
            skArc(sketch, "E32.27.2", {"start": v(6.76, 8.16) * mm, "mid": v(6.76, 8.08) * mm, "end": v(6.8, 8) * mm});
            skLineSegment(sketch, "E32.27.3", {"start": v(6.8, 8) * mm, "end": v(7.03, 7.8) * mm});
            skLineSegment(sketch, "E32.27.4", {"start": v(7.25, 7.6) * mm, "end": v(7.03, 7.8) * mm});
            skArc(sketch, "E32.27.5", {"start": v(7.41, 7.58) * mm, "mid": v(7.33, 7.56) * mm, "end": v(7.25, 7.6) * mm});
            skLineSegment(sketch, "E32.27.6", {"start": v(8.29, 7.98) * mm, "end": v(7.41, 7.58) * mm});
            skLineSegment(sketch, "E32.27.7", {"start": v(8.55, 7.7) * mm, "end": v(8.29, 7.98) * mm});
            skLineSegment(sketch, "E32.28.0", {"start": v(4.68, 10.5) * mm, "end": v(5.03, 10.35) * mm});
            skLineSegment(sketch, "E32.28.1", {"start": v(5.03, 10.35) * mm, "end": v(4.92, 9.4) * mm});
            skArc(sketch, "E32.28.2", {"start": v(4.92, 9.4) * mm, "mid": v(4.93, 9.3) * mm, "end": v(4.99, 9.24) * mm});
            skLineSegment(sketch, "E32.28.3", {"start": v(4.99, 9.24) * mm, "end": v(5.25, 9.1) * mm});
            skLineSegment(sketch, "E32.28.4", {"start": v(5.51, 8.94) * mm, "end": v(5.25, 9.1) * mm});
            skArc(sketch, "E32.28.5", {"start": v(5.68, 8.95) * mm, "mid": v(5.6, 8.92) * mm, "end": v(5.51, 8.94) * mm});
            skLineSegment(sketch, "E32.28.6", {"start": v(6.45, 9.53) * mm, "end": v(5.68, 8.95) * mm});
            skLineSegment(sketch, "E32.28.7", {"start": v(6.76, 9.3) * mm, "end": v(6.45, 9.53) * mm});
            skLineSegment(sketch, "E32.29.0", {"start": v(2.4, 11.25) * mm, "end": v(2.77, 11.17) * mm});
            skLineSegment(sketch, "E32.29.1", {"start": v(2.77, 11.17) * mm, "end": v(2.86, 10.2) * mm});
            skArc(sketch, "E32.29.2", {"start": v(2.86, 10.2) * mm, "mid": v(2.89, 10.13) * mm, "end": v(2.96, 10.08) * mm});
            skLineSegment(sketch, "E32.29.3", {"start": v(2.96, 10.08) * mm, "end": v(3.24, 9.99) * mm});
            skLineSegment(sketch, "E32.29.4", {"start": v(3.53, 9.9) * mm, "end": v(3.24, 9.99) * mm});
            skArc(sketch, "E32.29.5", {"start": v(3.7, 9.94) * mm, "mid": v(3.62, 9.9) * mm, "end": v(3.53, 9.9) * mm});
            skLineSegment(sketch, "E32.29.6", {"start": v(4.32, 10.66) * mm, "end": v(3.7, 9.94) * mm});
            skLineSegment(sketch, "E32.29.7", {"start": v(4.68, 10.5) * mm, "end": v(4.32, 10.66) * mm});
            skPoint(sketch, "E32.center", {"position": v(0, 0) * mm});
            skSolve(sketch);
        }
        {
            var Q0;
            Q0=qCreatedBy(makeId("Top.planeOp"),FACE);
            var sketch = newSketch(context, id + "F14", { "sketchPlane" : qUnion([Q0])});
            skCircle(sketch, "E33", {"center": v(0, 0) * mm, "radius": 12.5 * mm});
            skSolve(sketch);
        }
        {
            var Q0;
            Q0=qSketchRegion(id+"F14",true);
            extrude(context, id + "F15", {"entities" : qUnion([Q0]), "depth" : (getVariable(context, 'THICK')) * mm});
        }
        {
            var Q0;
            Q0=qSketchRegion(id+"F13",true);
            extrude(context, id + "F16", {"entities" : qUnion([Q0]), "operationType" : NewBodyOperationType.REMOVE, "depth" : 25 * mm});
        }
        {
            var Q0;
            Q0=qCreatedBy(makeId("Front.planeOp"),FACE);
            var sketch = newSketch(context, id + "F17", { "sketchPlane" : qUnion([Q0])});
            skLineSegment(sketch, "E34", {"start": v(0, 0) * mm, "end": v(0, 5.62) * mm});
            skSolve(sketch);
        }
        {
            var Q0;
            Q0=makeQuery(id+"F15.opExtrude","SWEPT_BODY",BODY,{"disambiguationData":[OSD([sQuery(id+"F14.wireOp",EDGE,"E33")])]});
            var Q1;
            Q1=sQuery(id+"F17.wireOp",EDGE,"E34");
            transform(context, id + "F18", {"entities" : qUnion([Q0]), "transformType" : TransformType.ROTATION, "transformAxis" : qUnion([Q1]), "angle" : 0 * degree, "makeCopy" : false});
        }
        {
            var Q0;
            Q0=qCreatedBy(makeId("Top.planeOp"),FACE);
            var sketch = newSketch(context, id + "F19", { "sketchPlane" : qUnion([Q0])});
            skCircle(sketch, "E35.cCircle", {"center": v(0, 0) * mm, "radius": 5.25 * mm, "construction": true});
            skLineSegment(sketch, "E35.0", {"start": v(-5.25, -9.1) * mm, "end": v(-5.25, 9.1) * mm});
            skLineSegment(sketch, "E35.1", {"start": v(-5.25, 9.1) * mm, "end": v(10.5, 0) * mm});
            skLineSegment(sketch, "E35.2", {"start": v(10.5, 0) * mm, "end": v(-5.25, -9.1) * mm});
            skPoint(sketch, "E35.0.midPoint", {"position": v(-5.25, 0) * mm});
            skLineSegment(sketch, "E36", {"start": v(0, 0) * mm, "end": v(10.5, 0) * mm});
            skLineSegment(sketch, "E37", {"start": v(0, 0) * mm, "end": v(-5.25, 9.1) * mm});
            skLineSegment(sketch, "E38", {"start": v(0, 0) * mm, "end": v(-5.25, -9.1) * mm});
            skSolve(sketch);
        }
        {
            var Q0;
            Q0=makeQuery(id+"F3.opExtrude","SWEPT_BODY",BODY,{"disambiguationData":[OSD([sQuery(id+"F2.wireOp",EDGE,"E6"),sQuery(id+"F2.wireOp",EDGE,"E7"),sQuery(id+"F2.wireOp",EDGE,"E8"),sQuery(id+"F2.wireOp",EDGE,"E9.filletArc"),sQuery(id+"F2.wireOp",EDGE,"E10.MirrorCS"),sQuery(id+"F2.wireOp",EDGE,"E11.MirrorCS"),sQuery(id+"F2.wireOp",EDGE,"E12.MirrorCS"),sQuery(id+"F2.wireOp",EDGE,"E13.MirrorCS"),sQuery(id+"F2.wireOp",EDGE,"E14.1.0"),sQuery(id+"F2.wireOp",EDGE,"E14.1.1"),sQuery(id+"F2.wireOp",EDGE,"E14.1.2"),sQuery(id+"F2.wireOp",EDGE,"E14.1.3"),sQuery(id+"F2.wireOp",EDGE,"E14.1.4"),sQuery(id+"F2.wireOp",EDGE,"E14.1.5"),sQuery(id+"F2.wireOp",EDGE,"E14.1.6"),sQuery(id+"F2.wireOp",EDGE,"E14.1.7"),sQuery(id+"F2.wireOp",EDGE,"E14.2.0"),sQuery(id+"F2.wireOp",EDGE,"E14.2.1"),sQuery(id+"F2.wireOp",EDGE,"E14.2.2"),sQuery(id+"F2.wireOp",EDGE,"E14.2.3"),sQuery(id+"F2.wireOp",EDGE,"E14.2.4"),sQuery(id+"F2.wireOp",EDGE,"E14.2.5"),sQuery(id+"F2.wireOp",EDGE,"E14.2.6"),sQuery(id+"F2.wireOp",EDGE,"E14.2.7"),sQuery(id+"F2.wireOp",EDGE,"E14.3.0"),sQuery(id+"F2.wireOp",EDGE,"E14.3.1"),sQuery(id+"F2.wireOp",EDGE,"E14.3.2"),sQuery(id+"F2.wireOp",EDGE,"E14.3.3"),sQuery(id+"F2.wireOp",EDGE,"E14.3.4"),sQuery(id+"F2.wireOp",EDGE,"E14.3.5"),sQuery(id+"F2.wireOp",EDGE,"E14.3.6"),sQuery(id+"F2.wireOp",EDGE,"E14.3.7"),sQuery(id+"F2.wireOp",EDGE,"E14.4.0"),sQuery(id+"F2.wireOp",EDGE,"E14.4.1"),sQuery(id+"F2.wireOp",EDGE,"E14.4.2"),sQuery(id+"F2.wireOp",EDGE,"E14.4.3"),sQuery(id+"F2.wireOp",EDGE,"E14.4.4"),sQuery(id+"F2.wireOp",EDGE,"E14.4.5"),sQuery(id+"F2.wireOp",EDGE,"E14.4.6"),sQuery(id+"F2.wireOp",EDGE,"E14.4.7"),sQuery(id+"F2.wireOp",EDGE,"E14.5.0"),sQuery(id+"F2.wireOp",EDGE,"E14.5.1"),sQuery(id+"F2.wireOp",EDGE,"E14.5.2"),sQuery(id+"F2.wireOp",EDGE,"E14.5.3"),sQuery(id+"F2.wireOp",EDGE,"E14.5.4"),sQuery(id+"F2.wireOp",EDGE,"E14.5.5"),sQuery(id+"F2.wireOp",EDGE,"E14.5.6"),sQuery(id+"F2.wireOp",EDGE,"E14.5.7"),sQuery(id+"F2.wireOp",EDGE,"E14.6.0"),sQuery(id+"F2.wireOp",EDGE,"E14.6.1"),sQuery(id+"F2.wireOp",EDGE,"E14.6.2"),sQuery(id+"F2.wireOp",EDGE,"E14.6.3"),sQuery(id+"F2.wireOp",EDGE,"E14.6.4"),sQuery(id+"F2.wireOp",EDGE,"E14.6.5"),sQuery(id+"F2.wireOp",EDGE,"E14.6.6"),sQuery(id+"F2.wireOp",EDGE,"E14.6.7"),sQuery(id+"F2.wireOp",EDGE,"E14.7.0"),sQuery(id+"F2.wireOp",EDGE,"E14.7.1"),sQuery(id+"F2.wireOp",EDGE,"E14.7.2"),sQuery(id+"F2.wireOp",EDGE,"E14.7.3"),sQuery(id+"F2.wireOp",EDGE,"E14.7.4"),sQuery(id+"F2.wireOp",EDGE,"E14.7.5"),sQuery(id+"F2.wireOp",EDGE,"E14.7.6"),sQuery(id+"F2.wireOp",EDGE,"E14.7.7"),sQuery(id+"F2.wireOp",EDGE,"E14.8.0"),sQuery(id+"F2.wireOp",EDGE,"E14.8.1"),sQuery(id+"F2.wireOp",EDGE,"E14.8.2"),sQuery(id+"F2.wireOp",EDGE,"E14.8.3"),sQuery(id+"F2.wireOp",EDGE,"E14.8.4"),sQuery(id+"F2.wireOp",EDGE,"E14.8.5"),sQuery(id+"F2.wireOp",EDGE,"E14.8.6"),sQuery(id+"F2.wireOp",EDGE,"E14.8.7"),sQuery(id+"F2.wireOp",EDGE,"E14.9.0"),sQuery(id+"F2.wireOp",EDGE,"E14.9.1"),sQuery(id+"F2.wireOp",EDGE,"E14.9.2"),sQuery(id+"F2.wireOp",EDGE,"E14.9.3"),sQuery(id+"F2.wireOp",EDGE,"E14.9.4"),sQuery(id+"F2.wireOp",EDGE,"E14.9.5"),sQuery(id+"F2.wireOp",EDGE,"E14.9.6"),sQuery(id+"F2.wireOp",EDGE,"E14.9.7")])]});
            var Q1;
            Q1=sQuery(id+"F17.wireOp",EDGE,"E34");
            transform(context, id + "F20", {"entities" : qUnion([Q0]), "transformType" : TransformType.ROTATION, "transformAxis" : qUnion([Q1]), "angle" : 0 * degree, "makeCopy" : false});
        }
        {
            var Q0;
            Q0=makeQuery(id+"F6.opPattern","COPY",BODY,{"derivedFrom":makeQuery(id+"F3.opExtrude","SWEPT_BODY",BODY,{"disambiguationData":[OSD([sQuery(id+"F2.wireOp",EDGE,"E6"),sQuery(id+"F2.wireOp",EDGE,"E7"),sQuery(id+"F2.wireOp",EDGE,"E8"),sQuery(id+"F2.wireOp",EDGE,"E9.filletArc"),sQuery(id+"F2.wireOp",EDGE,"E10.MirrorCS"),sQuery(id+"F2.wireOp",EDGE,"E11.MirrorCS"),sQuery(id+"F2.wireOp",EDGE,"E12.MirrorCS"),sQuery(id+"F2.wireOp",EDGE,"E13.MirrorCS"),sQuery(id+"F2.wireOp",EDGE,"E14.1.0"),sQuery(id+"F2.wireOp",EDGE,"E14.1.1"),sQuery(id+"F2.wireOp",EDGE,"E14.1.2"),sQuery(id+"F2.wireOp",EDGE,"E14.1.3"),sQuery(id+"F2.wireOp",EDGE,"E14.1.4"),sQuery(id+"F2.wireOp",EDGE,"E14.1.5"),sQuery(id+"F2.wireOp",EDGE,"E14.1.6"),sQuery(id+"F2.wireOp",EDGE,"E14.1.7"),sQuery(id+"F2.wireOp",EDGE,"E14.2.0"),sQuery(id+"F2.wireOp",EDGE,"E14.2.1"),sQuery(id+"F2.wireOp",EDGE,"E14.2.2"),sQuery(id+"F2.wireOp",EDGE,"E14.2.3"),sQuery(id+"F2.wireOp",EDGE,"E14.2.4"),sQuery(id+"F2.wireOp",EDGE,"E14.2.5"),sQuery(id+"F2.wireOp",EDGE,"E14.2.6"),sQuery(id+"F2.wireOp",EDGE,"E14.2.7"),sQuery(id+"F2.wireOp",EDGE,"E14.3.0"),sQuery(id+"F2.wireOp",EDGE,"E14.3.1"),sQuery(id+"F2.wireOp",EDGE,"E14.3.2"),sQuery(id+"F2.wireOp",EDGE,"E14.3.3"),sQuery(id+"F2.wireOp",EDGE,"E14.3.4"),sQuery(id+"F2.wireOp",EDGE,"E14.3.5"),sQuery(id+"F2.wireOp",EDGE,"E14.3.6"),sQuery(id+"F2.wireOp",EDGE,"E14.3.7"),sQuery(id+"F2.wireOp",EDGE,"E14.4.0"),sQuery(id+"F2.wireOp",EDGE,"E14.4.1"),sQuery(id+"F2.wireOp",EDGE,"E14.4.2"),sQuery(id+"F2.wireOp",EDGE,"E14.4.3"),sQuery(id+"F2.wireOp",EDGE,"E14.4.4"),sQuery(id+"F2.wireOp",EDGE,"E14.4.5"),sQuery(id+"F2.wireOp",EDGE,"E14.4.6"),sQuery(id+"F2.wireOp",EDGE,"E14.4.7"),sQuery(id+"F2.wireOp",EDGE,"E14.5.0"),sQuery(id+"F2.wireOp",EDGE,"E14.5.1"),sQuery(id+"F2.wireOp",EDGE,"E14.5.2"),sQuery(id+"F2.wireOp",EDGE,"E14.5.3"),sQuery(id+"F2.wireOp",EDGE,"E14.5.4"),sQuery(id+"F2.wireOp",EDGE,"E14.5.5"),sQuery(id+"F2.wireOp",EDGE,"E14.5.6"),sQuery(id+"F2.wireOp",EDGE,"E14.5.7"),sQuery(id+"F2.wireOp",EDGE,"E14.6.0"),sQuery(id+"F2.wireOp",EDGE,"E14.6.1"),sQuery(id+"F2.wireOp",EDGE,"E14.6.2"),sQuery(id+"F2.wireOp",EDGE,"E14.6.3"),sQuery(id+"F2.wireOp",EDGE,"E14.6.4"),sQuery(id+"F2.wireOp",EDGE,"E14.6.5"),sQuery(id+"F2.wireOp",EDGE,"E14.6.6"),sQuery(id+"F2.wireOp",EDGE,"E14.6.7"),sQuery(id+"F2.wireOp",EDGE,"E14.7.0"),sQuery(id+"F2.wireOp",EDGE,"E14.7.1"),sQuery(id+"F2.wireOp",EDGE,"E14.7.2"),sQuery(id+"F2.wireOp",EDGE,"E14.7.3"),sQuery(id+"F2.wireOp",EDGE,"E14.7.4"),sQuery(id+"F2.wireOp",EDGE,"E14.7.5"),sQuery(id+"F2.wireOp",EDGE,"E14.7.6"),sQuery(id+"F2.wireOp",EDGE,"E14.7.7"),sQuery(id+"F2.wireOp",EDGE,"E14.8.0"),sQuery(id+"F2.wireOp",EDGE,"E14.8.1"),sQuery(id+"F2.wireOp",EDGE,"E14.8.2"),sQuery(id+"F2.wireOp",EDGE,"E14.8.3"),sQuery(id+"F2.wireOp",EDGE,"E14.8.4"),sQuery(id+"F2.wireOp",EDGE,"E14.8.5"),sQuery(id+"F2.wireOp",EDGE,"E14.8.6"),sQuery(id+"F2.wireOp",EDGE,"E14.8.7"),sQuery(id+"F2.wireOp",EDGE,"E14.9.0"),sQuery(id+"F2.wireOp",EDGE,"E14.9.1"),sQuery(id+"F2.wireOp",EDGE,"E14.9.2"),sQuery(id+"F2.wireOp",EDGE,"E14.9.3"),sQuery(id+"F2.wireOp",EDGE,"E14.9.4"),sQuery(id+"F2.wireOp",EDGE,"E14.9.5"),sQuery(id+"F2.wireOp",EDGE,"E14.9.6"),sQuery(id+"F2.wireOp",EDGE,"E14.9.7")])]}),"instanceName":"1"});
            var Q1;
            Q1=sQuery(id+"F17.wireOp",EDGE,"E34");
            transform(context, id + "F21", {"entities" : qUnion([Q0]), "transformType" : TransformType.ROTATION, "transformAxis" : qUnion([Q1]), "angle" : 35.5 * degree, "makeCopy" : false});
        }
        {
            var Q0;
            Q0=makeQuery(id+"F11.opPattern","COPY",BODY,{"derivedFrom":makeQuery(id+"F6.opPattern","COPY",BODY,{"derivedFrom":makeQuery(id+"F3.opExtrude","SWEPT_BODY",BODY,{"disambiguationData":[OSD([sQuery(id+"F2.wireOp",EDGE,"E6"),sQuery(id+"F2.wireOp",EDGE,"E7"),sQuery(id+"F2.wireOp",EDGE,"E8"),sQuery(id+"F2.wireOp",EDGE,"E9.filletArc"),sQuery(id+"F2.wireOp",EDGE,"E10.MirrorCS"),sQuery(id+"F2.wireOp",EDGE,"E11.MirrorCS"),sQuery(id+"F2.wireOp",EDGE,"E12.MirrorCS"),sQuery(id+"F2.wireOp",EDGE,"E13.MirrorCS"),sQuery(id+"F2.wireOp",EDGE,"E14.1.0"),sQuery(id+"F2.wireOp",EDGE,"E14.1.1"),sQuery(id+"F2.wireOp",EDGE,"E14.1.2"),sQuery(id+"F2.wireOp",EDGE,"E14.1.3"),sQuery(id+"F2.wireOp",EDGE,"E14.1.4"),sQuery(id+"F2.wireOp",EDGE,"E14.1.5"),sQuery(id+"F2.wireOp",EDGE,"E14.1.6"),sQuery(id+"F2.wireOp",EDGE,"E14.1.7"),sQuery(id+"F2.wireOp",EDGE,"E14.2.0"),sQuery(id+"F2.wireOp",EDGE,"E14.2.1"),sQuery(id+"F2.wireOp",EDGE,"E14.2.2"),sQuery(id+"F2.wireOp",EDGE,"E14.2.3"),sQuery(id+"F2.wireOp",EDGE,"E14.2.4"),sQuery(id+"F2.wireOp",EDGE,"E14.2.5"),sQuery(id+"F2.wireOp",EDGE,"E14.2.6"),sQuery(id+"F2.wireOp",EDGE,"E14.2.7"),sQuery(id+"F2.wireOp",EDGE,"E14.3.0"),sQuery(id+"F2.wireOp",EDGE,"E14.3.1"),sQuery(id+"F2.wireOp",EDGE,"E14.3.2"),sQuery(id+"F2.wireOp",EDGE,"E14.3.3"),sQuery(id+"F2.wireOp",EDGE,"E14.3.4"),sQuery(id+"F2.wireOp",EDGE,"E14.3.5"),sQuery(id+"F2.wireOp",EDGE,"E14.3.6"),sQuery(id+"F2.wireOp",EDGE,"E14.3.7"),sQuery(id+"F2.wireOp",EDGE,"E14.4.0"),sQuery(id+"F2.wireOp",EDGE,"E14.4.1"),sQuery(id+"F2.wireOp",EDGE,"E14.4.2"),sQuery(id+"F2.wireOp",EDGE,"E14.4.3"),sQuery(id+"F2.wireOp",EDGE,"E14.4.4"),sQuery(id+"F2.wireOp",EDGE,"E14.4.5"),sQuery(id+"F2.wireOp",EDGE,"E14.4.6"),sQuery(id+"F2.wireOp",EDGE,"E14.4.7"),sQuery(id+"F2.wireOp",EDGE,"E14.5.0"),sQuery(id+"F2.wireOp",EDGE,"E14.5.1"),sQuery(id+"F2.wireOp",EDGE,"E14.5.2"),sQuery(id+"F2.wireOp",EDGE,"E14.5.3"),sQuery(id+"F2.wireOp",EDGE,"E14.5.4"),sQuery(id+"F2.wireOp",EDGE,"E14.5.5"),sQuery(id+"F2.wireOp",EDGE,"E14.5.6"),sQuery(id+"F2.wireOp",EDGE,"E14.5.7"),sQuery(id+"F2.wireOp",EDGE,"E14.6.0"),sQuery(id+"F2.wireOp",EDGE,"E14.6.1"),sQuery(id+"F2.wireOp",EDGE,"E14.6.2"),sQuery(id+"F2.wireOp",EDGE,"E14.6.3"),sQuery(id+"F2.wireOp",EDGE,"E14.6.4"),sQuery(id+"F2.wireOp",EDGE,"E14.6.5"),sQuery(id+"F2.wireOp",EDGE,"E14.6.6"),sQuery(id+"F2.wireOp",EDGE,"E14.6.7"),sQuery(id+"F2.wireOp",EDGE,"E14.7.0"),sQuery(id+"F2.wireOp",EDGE,"E14.7.1"),sQuery(id+"F2.wireOp",EDGE,"E14.7.2"),sQuery(id+"F2.wireOp",EDGE,"E14.7.3"),sQuery(id+"F2.wireOp",EDGE,"E14.7.4"),sQuery(id+"F2.wireOp",EDGE,"E14.7.5"),sQuery(id+"F2.wireOp",EDGE,"E14.7.6"),sQuery(id+"F2.wireOp",EDGE,"E14.7.7"),sQuery(id+"F2.wireOp",EDGE,"E14.8.0"),sQuery(id+"F2.wireOp",EDGE,"E14.8.1"),sQuery(id+"F2.wireOp",EDGE,"E14.8.2"),sQuery(id+"F2.wireOp",EDGE,"E14.8.3"),sQuery(id+"F2.wireOp",EDGE,"E14.8.4"),sQuery(id+"F2.wireOp",EDGE,"E14.8.5"),sQuery(id+"F2.wireOp",EDGE,"E14.8.6"),sQuery(id+"F2.wireOp",EDGE,"E14.8.7"),sQuery(id+"F2.wireOp",EDGE,"E14.9.0"),sQuery(id+"F2.wireOp",EDGE,"E14.9.1"),sQuery(id+"F2.wireOp",EDGE,"E14.9.2"),sQuery(id+"F2.wireOp",EDGE,"E14.9.3"),sQuery(id+"F2.wireOp",EDGE,"E14.9.4"),sQuery(id+"F2.wireOp",EDGE,"E14.9.5"),sQuery(id+"F2.wireOp",EDGE,"E14.9.6"),sQuery(id+"F2.wireOp",EDGE,"E14.9.7")])]}),"instanceName":"1"}),"instanceName":"1"});
            var Q1;
            Q1=sQuery(id+"F17.wireOp",EDGE,"E34");
            transform(context, id + "F22", {"entities" : qUnion([Q0]), "transformType" : TransformType.ROTATION, "transformAxis" : qUnion([Q1]), "angle" : 0 * degree, "makeCopy" : false});
        }
        {
            var Q0;
            Q0=makeQuery(id+"F3.opExtrude","SWEPT_BODY",BODY,{"disambiguationData":[OSD([sQuery(id+"F2.wireOp",EDGE,"E6"),sQuery(id+"F2.wireOp",EDGE,"E7"),sQuery(id+"F2.wireOp",EDGE,"E8"),sQuery(id+"F2.wireOp",EDGE,"E9.filletArc"),sQuery(id+"F2.wireOp",EDGE,"E10.MirrorCS"),sQuery(id+"F2.wireOp",EDGE,"E11.MirrorCS"),sQuery(id+"F2.wireOp",EDGE,"E12.MirrorCS"),sQuery(id+"F2.wireOp",EDGE,"E13.MirrorCS"),sQuery(id+"F2.wireOp",EDGE,"E14.1.0"),sQuery(id+"F2.wireOp",EDGE,"E14.1.1"),sQuery(id+"F2.wireOp",EDGE,"E14.1.2"),sQuery(id+"F2.wireOp",EDGE,"E14.1.3"),sQuery(id+"F2.wireOp",EDGE,"E14.1.4"),sQuery(id+"F2.wireOp",EDGE,"E14.1.5"),sQuery(id+"F2.wireOp",EDGE,"E14.1.6"),sQuery(id+"F2.wireOp",EDGE,"E14.1.7"),sQuery(id+"F2.wireOp",EDGE,"E14.2.0"),sQuery(id+"F2.wireOp",EDGE,"E14.2.1"),sQuery(id+"F2.wireOp",EDGE,"E14.2.2"),sQuery(id+"F2.wireOp",EDGE,"E14.2.3"),sQuery(id+"F2.wireOp",EDGE,"E14.2.4"),sQuery(id+"F2.wireOp",EDGE,"E14.2.5"),sQuery(id+"F2.wireOp",EDGE,"E14.2.6"),sQuery(id+"F2.wireOp",EDGE,"E14.2.7"),sQuery(id+"F2.wireOp",EDGE,"E14.3.0"),sQuery(id+"F2.wireOp",EDGE,"E14.3.1"),sQuery(id+"F2.wireOp",EDGE,"E14.3.2"),sQuery(id+"F2.wireOp",EDGE,"E14.3.3"),sQuery(id+"F2.wireOp",EDGE,"E14.3.4"),sQuery(id+"F2.wireOp",EDGE,"E14.3.5"),sQuery(id+"F2.wireOp",EDGE,"E14.3.6"),sQuery(id+"F2.wireOp",EDGE,"E14.3.7"),sQuery(id+"F2.wireOp",EDGE,"E14.4.0"),sQuery(id+"F2.wireOp",EDGE,"E14.4.1"),sQuery(id+"F2.wireOp",EDGE,"E14.4.2"),sQuery(id+"F2.wireOp",EDGE,"E14.4.3"),sQuery(id+"F2.wireOp",EDGE,"E14.4.4"),sQuery(id+"F2.wireOp",EDGE,"E14.4.5"),sQuery(id+"F2.wireOp",EDGE,"E14.4.6"),sQuery(id+"F2.wireOp",EDGE,"E14.4.7"),sQuery(id+"F2.wireOp",EDGE,"E14.5.0"),sQuery(id+"F2.wireOp",EDGE,"E14.5.1"),sQuery(id+"F2.wireOp",EDGE,"E14.5.2"),sQuery(id+"F2.wireOp",EDGE,"E14.5.3"),sQuery(id+"F2.wireOp",EDGE,"E14.5.4"),sQuery(id+"F2.wireOp",EDGE,"E14.5.5"),sQuery(id+"F2.wireOp",EDGE,"E14.5.6"),sQuery(id+"F2.wireOp",EDGE,"E14.5.7"),sQuery(id+"F2.wireOp",EDGE,"E14.6.0"),sQuery(id+"F2.wireOp",EDGE,"E14.6.1"),sQuery(id+"F2.wireOp",EDGE,"E14.6.2"),sQuery(id+"F2.wireOp",EDGE,"E14.6.3"),sQuery(id+"F2.wireOp",EDGE,"E14.6.4"),sQuery(id+"F2.wireOp",EDGE,"E14.6.5"),sQuery(id+"F2.wireOp",EDGE,"E14.6.6"),sQuery(id+"F2.wireOp",EDGE,"E14.6.7"),sQuery(id+"F2.wireOp",EDGE,"E14.7.0"),sQuery(id+"F2.wireOp",EDGE,"E14.7.1"),sQuery(id+"F2.wireOp",EDGE,"E14.7.2"),sQuery(id+"F2.wireOp",EDGE,"E14.7.3"),sQuery(id+"F2.wireOp",EDGE,"E14.7.4"),sQuery(id+"F2.wireOp",EDGE,"E14.7.5"),sQuery(id+"F2.wireOp",EDGE,"E14.7.6"),sQuery(id+"F2.wireOp",EDGE,"E14.7.7"),sQuery(id+"F2.wireOp",EDGE,"E14.8.0"),sQuery(id+"F2.wireOp",EDGE,"E14.8.1"),sQuery(id+"F2.wireOp",EDGE,"E14.8.2"),sQuery(id+"F2.wireOp",EDGE,"E14.8.3"),sQuery(id+"F2.wireOp",EDGE,"E14.8.4"),sQuery(id+"F2.wireOp",EDGE,"E14.8.5"),sQuery(id+"F2.wireOp",EDGE,"E14.8.6"),sQuery(id+"F2.wireOp",EDGE,"E14.8.7"),sQuery(id+"F2.wireOp",EDGE,"E14.9.0"),sQuery(id+"F2.wireOp",EDGE,"E14.9.1"),sQuery(id+"F2.wireOp",EDGE,"E14.9.2"),sQuery(id+"F2.wireOp",EDGE,"E14.9.3"),sQuery(id+"F2.wireOp",EDGE,"E14.9.4"),sQuery(id+"F2.wireOp",EDGE,"E14.9.5"),sQuery(id+"F2.wireOp",EDGE,"E14.9.6"),sQuery(id+"F2.wireOp",EDGE,"E14.9.7")])]});
            var Q1;
            Q1=sQuery(id+"F19.wireOp",EDGE,"E36");
            transform(context, id + "F23", {"entities" : qUnion([Q0]), "transformType" : TransformType.TRANSLATION_ENTITY, "oppositeDirectionEntity" : false, "transformLine" : qUnion([Q1]), "makeCopy" : false});
        }
        {
            var Q0;
            Q0=makeQuery(id+"F6.opPattern","COPY",BODY,{"derivedFrom":makeQuery(id+"F3.opExtrude","SWEPT_BODY",BODY,{"disambiguationData":[OSD([sQuery(id+"F2.wireOp",EDGE,"E6"),sQuery(id+"F2.wireOp",EDGE,"E7"),sQuery(id+"F2.wireOp",EDGE,"E8"),sQuery(id+"F2.wireOp",EDGE,"E9.filletArc"),sQuery(id+"F2.wireOp",EDGE,"E10.MirrorCS"),sQuery(id+"F2.wireOp",EDGE,"E11.MirrorCS"),sQuery(id+"F2.wireOp",EDGE,"E12.MirrorCS"),sQuery(id+"F2.wireOp",EDGE,"E13.MirrorCS"),sQuery(id+"F2.wireOp",EDGE,"E14.1.0"),sQuery(id+"F2.wireOp",EDGE,"E14.1.1"),sQuery(id+"F2.wireOp",EDGE,"E14.1.2"),sQuery(id+"F2.wireOp",EDGE,"E14.1.3"),sQuery(id+"F2.wireOp",EDGE,"E14.1.4"),sQuery(id+"F2.wireOp",EDGE,"E14.1.5"),sQuery(id+"F2.wireOp",EDGE,"E14.1.6"),sQuery(id+"F2.wireOp",EDGE,"E14.1.7"),sQuery(id+"F2.wireOp",EDGE,"E14.2.0"),sQuery(id+"F2.wireOp",EDGE,"E14.2.1"),sQuery(id+"F2.wireOp",EDGE,"E14.2.2"),sQuery(id+"F2.wireOp",EDGE,"E14.2.3"),sQuery(id+"F2.wireOp",EDGE,"E14.2.4"),sQuery(id+"F2.wireOp",EDGE,"E14.2.5"),sQuery(id+"F2.wireOp",EDGE,"E14.2.6"),sQuery(id+"F2.wireOp",EDGE,"E14.2.7"),sQuery(id+"F2.wireOp",EDGE,"E14.3.0"),sQuery(id+"F2.wireOp",EDGE,"E14.3.1"),sQuery(id+"F2.wireOp",EDGE,"E14.3.2"),sQuery(id+"F2.wireOp",EDGE,"E14.3.3"),sQuery(id+"F2.wireOp",EDGE,"E14.3.4"),sQuery(id+"F2.wireOp",EDGE,"E14.3.5"),sQuery(id+"F2.wireOp",EDGE,"E14.3.6"),sQuery(id+"F2.wireOp",EDGE,"E14.3.7"),sQuery(id+"F2.wireOp",EDGE,"E14.4.0"),sQuery(id+"F2.wireOp",EDGE,"E14.4.1"),sQuery(id+"F2.wireOp",EDGE,"E14.4.2"),sQuery(id+"F2.wireOp",EDGE,"E14.4.3"),sQuery(id+"F2.wireOp",EDGE,"E14.4.4"),sQuery(id+"F2.wireOp",EDGE,"E14.4.5"),sQuery(id+"F2.wireOp",EDGE,"E14.4.6"),sQuery(id+"F2.wireOp",EDGE,"E14.4.7"),sQuery(id+"F2.wireOp",EDGE,"E14.5.0"),sQuery(id+"F2.wireOp",EDGE,"E14.5.1"),sQuery(id+"F2.wireOp",EDGE,"E14.5.2"),sQuery(id+"F2.wireOp",EDGE,"E14.5.3"),sQuery(id+"F2.wireOp",EDGE,"E14.5.4"),sQuery(id+"F2.wireOp",EDGE,"E14.5.5"),sQuery(id+"F2.wireOp",EDGE,"E14.5.6"),sQuery(id+"F2.wireOp",EDGE,"E14.5.7"),sQuery(id+"F2.wireOp",EDGE,"E14.6.0"),sQuery(id+"F2.wireOp",EDGE,"E14.6.1"),sQuery(id+"F2.wireOp",EDGE,"E14.6.2"),sQuery(id+"F2.wireOp",EDGE,"E14.6.3"),sQuery(id+"F2.wireOp",EDGE,"E14.6.4"),sQuery(id+"F2.wireOp",EDGE,"E14.6.5"),sQuery(id+"F2.wireOp",EDGE,"E14.6.6"),sQuery(id+"F2.wireOp",EDGE,"E14.6.7"),sQuery(id+"F2.wireOp",EDGE,"E14.7.0"),sQuery(id+"F2.wireOp",EDGE,"E14.7.1"),sQuery(id+"F2.wireOp",EDGE,"E14.7.2"),sQuery(id+"F2.wireOp",EDGE,"E14.7.3"),sQuery(id+"F2.wireOp",EDGE,"E14.7.4"),sQuery(id+"F2.wireOp",EDGE,"E14.7.5"),sQuery(id+"F2.wireOp",EDGE,"E14.7.6"),sQuery(id+"F2.wireOp",EDGE,"E14.7.7"),sQuery(id+"F2.wireOp",EDGE,"E14.8.0"),sQuery(id+"F2.wireOp",EDGE,"E14.8.1"),sQuery(id+"F2.wireOp",EDGE,"E14.8.2"),sQuery(id+"F2.wireOp",EDGE,"E14.8.3"),sQuery(id+"F2.wireOp",EDGE,"E14.8.4"),sQuery(id+"F2.wireOp",EDGE,"E14.8.5"),sQuery(id+"F2.wireOp",EDGE,"E14.8.6"),sQuery(id+"F2.wireOp",EDGE,"E14.8.7"),sQuery(id+"F2.wireOp",EDGE,"E14.9.0"),sQuery(id+"F2.wireOp",EDGE,"E14.9.1"),sQuery(id+"F2.wireOp",EDGE,"E14.9.2"),sQuery(id+"F2.wireOp",EDGE,"E14.9.3"),sQuery(id+"F2.wireOp",EDGE,"E14.9.4"),sQuery(id+"F2.wireOp",EDGE,"E14.9.5"),sQuery(id+"F2.wireOp",EDGE,"E14.9.6"),sQuery(id+"F2.wireOp",EDGE,"E14.9.7")])]}),"instanceName":"1"});
            var Q1;
            Q1=sQuery(id+"F19.wireOp",EDGE,"E37");
            transform(context, id + "F24", {"entities" : qUnion([Q0]), "transformType" : TransformType.TRANSLATION_ENTITY, "oppositeDirectionEntity" : false, "transformLine" : qUnion([Q1]), "makeCopy" : false});
        }
        {
            var Q0;
            Q0=makeQuery(id+"F11.opPattern","COPY",BODY,{"derivedFrom":makeQuery(id+"F6.opPattern","COPY",BODY,{"derivedFrom":makeQuery(id+"F3.opExtrude","SWEPT_BODY",BODY,{"disambiguationData":[OSD([sQuery(id+"F2.wireOp",EDGE,"E6"),sQuery(id+"F2.wireOp",EDGE,"E7"),sQuery(id+"F2.wireOp",EDGE,"E8"),sQuery(id+"F2.wireOp",EDGE,"E9.filletArc"),sQuery(id+"F2.wireOp",EDGE,"E10.MirrorCS"),sQuery(id+"F2.wireOp",EDGE,"E11.MirrorCS"),sQuery(id+"F2.wireOp",EDGE,"E12.MirrorCS"),sQuery(id+"F2.wireOp",EDGE,"E13.MirrorCS"),sQuery(id+"F2.wireOp",EDGE,"E14.1.0"),sQuery(id+"F2.wireOp",EDGE,"E14.1.1"),sQuery(id+"F2.wireOp",EDGE,"E14.1.2"),sQuery(id+"F2.wireOp",EDGE,"E14.1.3"),sQuery(id+"F2.wireOp",EDGE,"E14.1.4"),sQuery(id+"F2.wireOp",EDGE,"E14.1.5"),sQuery(id+"F2.wireOp",EDGE,"E14.1.6"),sQuery(id+"F2.wireOp",EDGE,"E14.1.7"),sQuery(id+"F2.wireOp",EDGE,"E14.2.0"),sQuery(id+"F2.wireOp",EDGE,"E14.2.1"),sQuery(id+"F2.wireOp",EDGE,"E14.2.2"),sQuery(id+"F2.wireOp",EDGE,"E14.2.3"),sQuery(id+"F2.wireOp",EDGE,"E14.2.4"),sQuery(id+"F2.wireOp",EDGE,"E14.2.5"),sQuery(id+"F2.wireOp",EDGE,"E14.2.6"),sQuery(id+"F2.wireOp",EDGE,"E14.2.7"),sQuery(id+"F2.wireOp",EDGE,"E14.3.0"),sQuery(id+"F2.wireOp",EDGE,"E14.3.1"),sQuery(id+"F2.wireOp",EDGE,"E14.3.2"),sQuery(id+"F2.wireOp",EDGE,"E14.3.3"),sQuery(id+"F2.wireOp",EDGE,"E14.3.4"),sQuery(id+"F2.wireOp",EDGE,"E14.3.5"),sQuery(id+"F2.wireOp",EDGE,"E14.3.6"),sQuery(id+"F2.wireOp",EDGE,"E14.3.7"),sQuery(id+"F2.wireOp",EDGE,"E14.4.0"),sQuery(id+"F2.wireOp",EDGE,"E14.4.1"),sQuery(id+"F2.wireOp",EDGE,"E14.4.2"),sQuery(id+"F2.wireOp",EDGE,"E14.4.3"),sQuery(id+"F2.wireOp",EDGE,"E14.4.4"),sQuery(id+"F2.wireOp",EDGE,"E14.4.5"),sQuery(id+"F2.wireOp",EDGE,"E14.4.6"),sQuery(id+"F2.wireOp",EDGE,"E14.4.7"),sQuery(id+"F2.wireOp",EDGE,"E14.5.0"),sQuery(id+"F2.wireOp",EDGE,"E14.5.1"),sQuery(id+"F2.wireOp",EDGE,"E14.5.2"),sQuery(id+"F2.wireOp",EDGE,"E14.5.3"),sQuery(id+"F2.wireOp",EDGE,"E14.5.4"),sQuery(id+"F2.wireOp",EDGE,"E14.5.5"),sQuery(id+"F2.wireOp",EDGE,"E14.5.6"),sQuery(id+"F2.wireOp",EDGE,"E14.5.7"),sQuery(id+"F2.wireOp",EDGE,"E14.6.0"),sQuery(id+"F2.wireOp",EDGE,"E14.6.1"),sQuery(id+"F2.wireOp",EDGE,"E14.6.2"),sQuery(id+"F2.wireOp",EDGE,"E14.6.3"),sQuery(id+"F2.wireOp",EDGE,"E14.6.4"),sQuery(id+"F2.wireOp",EDGE,"E14.6.5"),sQuery(id+"F2.wireOp",EDGE,"E14.6.6"),sQuery(id+"F2.wireOp",EDGE,"E14.6.7"),sQuery(id+"F2.wireOp",EDGE,"E14.7.0"),sQuery(id+"F2.wireOp",EDGE,"E14.7.1"),sQuery(id+"F2.wireOp",EDGE,"E14.7.2"),sQuery(id+"F2.wireOp",EDGE,"E14.7.3"),sQuery(id+"F2.wireOp",EDGE,"E14.7.4"),sQuery(id+"F2.wireOp",EDGE,"E14.7.5"),sQuery(id+"F2.wireOp",EDGE,"E14.7.6"),sQuery(id+"F2.wireOp",EDGE,"E14.7.7"),sQuery(id+"F2.wireOp",EDGE,"E14.8.0"),sQuery(id+"F2.wireOp",EDGE,"E14.8.1"),sQuery(id+"F2.wireOp",EDGE,"E14.8.2"),sQuery(id+"F2.wireOp",EDGE,"E14.8.3"),sQuery(id+"F2.wireOp",EDGE,"E14.8.4"),sQuery(id+"F2.wireOp",EDGE,"E14.8.5"),sQuery(id+"F2.wireOp",EDGE,"E14.8.6"),sQuery(id+"F2.wireOp",EDGE,"E14.8.7"),sQuery(id+"F2.wireOp",EDGE,"E14.9.0"),sQuery(id+"F2.wireOp",EDGE,"E14.9.1"),sQuery(id+"F2.wireOp",EDGE,"E14.9.2"),sQuery(id+"F2.wireOp",EDGE,"E14.9.3"),sQuery(id+"F2.wireOp",EDGE,"E14.9.4"),sQuery(id+"F2.wireOp",EDGE,"E14.9.5"),sQuery(id+"F2.wireOp",EDGE,"E14.9.6"),sQuery(id+"F2.wireOp",EDGE,"E14.9.7")])]}),"instanceName":"1"}),"instanceName":"1"});
            var Q1;
            Q1=sQuery(id+"F19.wireOp",EDGE,"E38");
            transform(context, id + "F25", {"entities" : qUnion([Q0]), "transformType" : TransformType.TRANSLATION_ENTITY, "oppositeDirectionEntity" : false, "transformLine" : qUnion([Q1]), "makeCopy" : false});
        }
        {
            var Q0;
            Q0=qCreatedBy(makeId("Top.planeOp"),FACE);
            cPlane(context, id + "F26", {"entities" : qUnion([Q0]), "cplaneType" : CPlaneType.OFFSET, "offset" : 0.3 * mm, "oppositeDirection" : true, "width" : 150 * mm, "height" : 150 * mm});
        }
        {
            var Q0;
            Q0=qCreatedBy(id+"F26.planeOp",FACE);
            var sketch = newSketch(context, id + "F27", { "sketchPlane" : qUnion([Q0])});
            skCircle(sketch, "E39", {"center": v(0, 0) * mm, "radius": 13 * mm});
            skCircle(sketch, "E40", {"center": v(0, 0) * mm, "radius": 8.5 * mm});
            skSolve(sketch);
        }
        {
            var Q0;
            Q0=qSketchRegion(id+"F27",true);
            extrude(context, id + "F28", {"entities" : qUnion([Q0]), "oppositeDirection" : true, "depth" : 1.6 * mm});
        }
        {
            var Q0;
            Q0=makeQuery(id+"F28.opExtrude","CAP_FACE",FACE,{"disambiguationData":[OSD([sQuery(id+"F27.wireOp",EDGE,"E39"),sQuery(id+"F27.wireOp",EDGE,"E40")])],"isStart":true});
            var sketch = newSketch(context, id + "F29", { "sketchPlane" : qUnion([Q0])});
            skCircle(sketch, "E41.cCircle", {"center": v(0, 0) * mm, "radius": 10.58 * mm, "construction": true});
            skLineSegment(sketch, "E41.0", {"start": v(-10.58, -18.32) * mm, "end": v(-10.58, 18.32) * mm});
            skLineSegment(sketch, "E41.1", {"start": v(-10.58, 18.32) * mm, "end": v(21.15, 0) * mm});
            skLineSegment(sketch, "E41.2", {"start": v(21.15, 0) * mm, "end": v(-10.58, -18.32) * mm});
            skPoint(sketch, "E41.0.midPoint", {"position": v(-10.58, 0) * mm});
            skSolve(sketch);
        }
        {
            var Q0;
            Q0=qSketchRegion(id+"F29",true);
            extrude(context, id + "F30", {"entities" : qUnion([Q0]), "operationType" : NewBodyOperationType.INTERSECT, "oppositeDirection" : true, "depth" : 25 * mm});
        }
        {
            var Q0;
            Q0=makeQuery(id+"F28.opExtrude","CAP_FACE",FACE,{"disambiguationData":[OSD([sQuery(id+"F27.wireOp",EDGE,"E39"),sQuery(id+"F27.wireOp",EDGE,"E40")])],"isStart":true});
            var sketch = newSketch(context, id + "F31", { "sketchPlane" : qUnion([Q0])});
            skCircle(sketch, "E42", {"center": v(-5.25, 9.1) * mm, "radius": 1 * mm});
            skCircle(sketch, "E43", {"center": v(-5.25, -9.1) * mm, "radius": 1 * mm});
            skCircle(sketch, "E44", {"center": v(10.5, 0) * mm, "radius": 1 * mm});
            skSolve(sketch);
        }
        {
            var Q0;
            Q0=qSketchRegion(id+"F31",true);
            extrude(context, id + "F32", {"entities" : qUnion([Q0]), "operationType" : NewBodyOperationType.REMOVE, "oppositeDirection" : true, "depth" : 25 * mm});
        }
        {
            var Q0;
            Q0=makeQuery(id+"F28.opExtrude","SWEPT_BODY",BODY,{"disambiguationData":[OSD([sQuery(id+"F27.wireOp",EDGE,"E39"),sQuery(id+"F27.wireOp",EDGE,"E40")])]});
            var Q1;
            Q1=sQuery(id+"F17.wireOp",EDGE,"E34");
            transform(context, id + "F33", {"entities" : qUnion([Q0]), "transformType" : TransformType.ROTATION, "transformAxis" : qUnion([Q1]), "angle" : 30 * degree, "makeCopy" : true});
        }
        {
            var Q0;
            Q0=qCreatedBy(makeId("Top.planeOp"),FACE);
            var sketch = newSketch(context, id + "F34", { "sketchPlane" : qUnion([Q0])});
            skCircle(sketch, "E45", {"center": v(0, 0) * mm, "radius": 7 * mm, "construction": true});
            skCircle(sketch, "E46.0", {"center": v(0, 0) * mm, "radius": 6.5 * mm, "construction": true});
            skCircle(sketch, "E47.0", {"center": v(0, 0) * mm, "radius": 6 * mm, "construction": true});
            skSolve(sketch);
        }
        {
            var Q0;
            Q0=qCreatedBy(makeId("Top.planeOp"),FACE);
            var sketch = newSketch(context, id + "F35", { "sketchPlane" : qUnion([Q0])});
            skLineSegment(sketch, "E48", {"start": v(0, 14.52) * mm, "end": v(0, 0) * mm, "construction": true});
            skLineSegment(sketch, "E49", {"start": v(0, 0) * mm, "end": v(2.35, 14.81) * mm, "construction": true});
            skLineSegment(sketch, "E50", {"start": v(1.13, 14.34) * mm, "end": v(0, 0) * mm, "construction": true});
            skLineSegment(sketch, "E51", {"start": v(0, 7) * mm, "end": v(0.3, 7) * mm});
            skLineSegment(sketch, "E52", {"start": v(0.5, 6.8) * mm, "end": v(0.52, 6) * mm});
            skLineSegment(sketch, "E53", {"start": v(0.52, 6) * mm, "end": v(0.94, 5.93) * mm});
            skPoint(sketch, "E54.visualSharp", {"position": v(0.5, 7) * mm});
            skArc(sketch, "E54.filletArc", {"start": v(0.5, 6.8) * mm, "mid": v(0.44, 6.94) * mm, "end": v(0.3, 7) * mm});
            skLineSegment(sketch, "E55.MirrorCS", {"start": v(1.36, 5.86) * mm, "end": v(0.94, 5.93) * mm});
            skLineSegment(sketch, "E56.MirrorCS", {"start": v(2.16, 6.66) * mm, "end": v(1.87, 6.75) * mm});
            skLineSegment(sketch, "E57.MirrorCS", {"start": v(1.62, 6.63) * mm, "end": v(1.36, 5.86) * mm});
            skArc(sketch, "E58.MirrorCS", {"start": v(1.62, 6.63) * mm, "mid": v(1.72, 6.74) * mm, "end": v(1.87, 6.75) * mm});
            skLineSegment(sketch, "E59.1.0", {"start": v(0, 7) * mm, "end": v(-0.3, 7) * mm});
            skLineSegment(sketch, "E59.1.1", {"start": v(-1.36, 5.86) * mm, "end": v(-0.94, 5.93) * mm});
            skLineSegment(sketch, "E59.1.2", {"start": v(-0.5, 6.8) * mm, "end": v(-0.52, 6) * mm});
            skLineSegment(sketch, "E59.1.3", {"start": v(-0.52, 6) * mm, "end": v(-0.94, 5.93) * mm});
            skArc(sketch, "E59.1.4", {"start": v(-0.5, 6.8) * mm, "mid": v(-0.44, 6.94) * mm, "end": v(-0.3, 7) * mm});
            skLineSegment(sketch, "E59.1.5", {"start": v(-1.62, 6.63) * mm, "end": v(-1.36, 5.86) * mm});
            skArc(sketch, "E59.1.6", {"start": v(-1.62, 6.63) * mm, "mid": v(-1.72, 6.74) * mm, "end": v(-1.87, 6.75) * mm});
            skLineSegment(sketch, "E59.1.7", {"start": v(-2.16, 6.66) * mm, "end": v(-1.87, 6.75) * mm});
            skLineSegment(sketch, "E59.2.0", {"start": v(-2.16, 6.66) * mm, "end": v(-2.45, 6.56) * mm});
            skLineSegment(sketch, "E59.2.1", {"start": v(-3.1, 5.15) * mm, "end": v(-2.72, 5.35) * mm});
            skLineSegment(sketch, "E59.2.2", {"start": v(-2.58, 6.32) * mm, "end": v(-2.35, 5.54) * mm});
            skLineSegment(sketch, "E59.2.3", {"start": v(-2.35, 5.54) * mm, "end": v(-2.72, 5.35) * mm});
            skArc(sketch, "E59.2.4", {"start": v(-2.58, 6.32) * mm, "mid": v(-2.57, 6.47) * mm, "end": v(-2.45, 6.56) * mm});
            skLineSegment(sketch, "E59.2.5", {"start": v(-3.6, 5.8) * mm, "end": v(-3.1, 5.15) * mm});
            skArc(sketch, "E59.2.6", {"start": v(-3.6, 5.8) * mm, "mid": v(-3.72, 5.88) * mm, "end": v(-3.87, 5.84) * mm});
            skLineSegment(sketch, "E59.2.7", {"start": v(-4.11, 5.66) * mm, "end": v(-3.87, 5.84) * mm});
            skLineSegment(sketch, "E59.3.0", {"start": v(-4.11, 5.66) * mm, "end": v(-4.36, 5.48) * mm});
            skLineSegment(sketch, "E59.3.1", {"start": v(-4.54, 3.94) * mm, "end": v(-4.24, 4.24) * mm});
            skLineSegment(sketch, "E59.3.2", {"start": v(-4.4, 5.2) * mm, "end": v(-3.94, 4.54) * mm});
            skLineSegment(sketch, "E59.3.3", {"start": v(-3.94, 4.54) * mm, "end": v(-4.24, 4.24) * mm});
            skArc(sketch, "E59.3.4", {"start": v(-4.4, 5.2) * mm, "mid": v(-4.44, 5.36) * mm, "end": v(-4.36, 5.48) * mm});
            skLineSegment(sketch, "E59.3.5", {"start": v(-5.2, 4.4) * mm, "end": v(-4.54, 3.94) * mm});
            skArc(sketch, "E59.3.6", {"start": v(-5.2, 4.4) * mm, "mid": v(-5.36, 4.44) * mm, "end": v(-5.48, 4.36) * mm});
            skLineSegment(sketch, "E59.3.7", {"start": v(-5.66, 4.11) * mm, "end": v(-5.48, 4.36) * mm});
            skLineSegment(sketch, "E59.4.0", {"start": v(-5.66, 4.11) * mm, "end": v(-5.84, 3.87) * mm});
            skLineSegment(sketch, "E59.4.1", {"start": v(-5.54, 2.35) * mm, "end": v(-5.35, 2.72) * mm});
            skLineSegment(sketch, "E59.4.2", {"start": v(-5.8, 3.6) * mm, "end": v(-5.15, 3.1) * mm});
            skLineSegment(sketch, "E59.4.3", {"start": v(-5.15, 3.1) * mm, "end": v(-5.35, 2.72) * mm});
            skArc(sketch, "E59.4.4", {"start": v(-5.8, 3.6) * mm, "mid": v(-5.88, 3.72) * mm, "end": v(-5.84, 3.87) * mm});
            skLineSegment(sketch, "E59.4.5", {"start": v(-6.32, 2.58) * mm, "end": v(-5.54, 2.35) * mm});
            skArc(sketch, "E59.4.6", {"start": v(-6.32, 2.58) * mm, "mid": v(-6.47, 2.57) * mm, "end": v(-6.56, 2.45) * mm});
            skLineSegment(sketch, "E59.4.7", {"start": v(-6.66, 2.16) * mm, "end": v(-6.56, 2.45) * mm});
            skLineSegment(sketch, "E59.5.0", {"start": v(-6.66, 2.16) * mm, "end": v(-6.75, 1.87) * mm});
            skLineSegment(sketch, "E59.5.1", {"start": v(-6, 0.52) * mm, "end": v(-5.93, 0.94) * mm});
            skLineSegment(sketch, "E59.5.2", {"start": v(-6.63, 1.62) * mm, "end": v(-5.86, 1.36) * mm});
            skLineSegment(sketch, "E59.5.3", {"start": v(-5.86, 1.36) * mm, "end": v(-5.93, 0.94) * mm});
            skArc(sketch, "E59.5.4", {"start": v(-6.63, 1.62) * mm, "mid": v(-6.74, 1.72) * mm, "end": v(-6.75, 1.87) * mm});
            skLineSegment(sketch, "E59.5.5", {"start": v(-6.8, 0.5) * mm, "end": v(-6, 0.52) * mm});
            skArc(sketch, "E59.5.6", {"start": v(-6.8, 0.5) * mm, "mid": v(-6.94, 0.44) * mm, "end": v(-7, 0.3) * mm});
            skLineSegment(sketch, "E59.5.7", {"start": v(-7, 0) * mm, "end": v(-7, 0.3) * mm});
            skLineSegment(sketch, "E59.6.0", {"start": v(-7, 0) * mm, "end": v(-7, -0.3) * mm});
            skLineSegment(sketch, "E59.6.1", {"start": v(-5.86, -1.36) * mm, "end": v(-5.93, -0.94) * mm});
            skLineSegment(sketch, "E59.6.2", {"start": v(-6.8, -0.5) * mm, "end": v(-6, -0.52) * mm});
            skLineSegment(sketch, "E59.6.3", {"start": v(-6, -0.52) * mm, "end": v(-5.93, -0.94) * mm});
            skArc(sketch, "E59.6.4", {"start": v(-6.8, -0.5) * mm, "mid": v(-6.94, -0.44) * mm, "end": v(-7, -0.3) * mm});
            skLineSegment(sketch, "E59.6.5", {"start": v(-6.63, -1.62) * mm, "end": v(-5.86, -1.36) * mm});
            skArc(sketch, "E59.6.6", {"start": v(-6.63, -1.62) * mm, "mid": v(-6.74, -1.72) * mm, "end": v(-6.75, -1.87) * mm});
            skLineSegment(sketch, "E59.6.7", {"start": v(-6.66, -2.16) * mm, "end": v(-6.75, -1.87) * mm});
            skLineSegment(sketch, "E59.7.0", {"start": v(-6.66, -2.16) * mm, "end": v(-6.56, -2.45) * mm});
            skLineSegment(sketch, "E59.7.1", {"start": v(-5.15, -3.1) * mm, "end": v(-5.35, -2.72) * mm});
            skLineSegment(sketch, "E59.7.2", {"start": v(-6.32, -2.58) * mm, "end": v(-5.54, -2.35) * mm});
            skLineSegment(sketch, "E59.7.3", {"start": v(-5.54, -2.35) * mm, "end": v(-5.35, -2.72) * mm});
            skArc(sketch, "E59.7.4", {"start": v(-6.32, -2.58) * mm, "mid": v(-6.47, -2.57) * mm, "end": v(-6.56, -2.45) * mm});
            skLineSegment(sketch, "E59.7.5", {"start": v(-5.8, -3.6) * mm, "end": v(-5.15, -3.1) * mm});
            skArc(sketch, "E59.7.6", {"start": v(-5.8, -3.6) * mm, "mid": v(-5.88, -3.72) * mm, "end": v(-5.84, -3.87) * mm});
            skLineSegment(sketch, "E59.7.7", {"start": v(-5.66, -4.11) * mm, "end": v(-5.84, -3.87) * mm});
            skLineSegment(sketch, "E59.8.0", {"start": v(-5.66, -4.11) * mm, "end": v(-5.48, -4.36) * mm});
            skLineSegment(sketch, "E59.8.1", {"start": v(-3.94, -4.54) * mm, "end": v(-4.24, -4.24) * mm});
            skLineSegment(sketch, "E59.8.2", {"start": v(-5.2, -4.4) * mm, "end": v(-4.54, -3.94) * mm});
            skLineSegment(sketch, "E59.8.3", {"start": v(-4.54, -3.94) * mm, "end": v(-4.24, -4.24) * mm});
            skArc(sketch, "E59.8.4", {"start": v(-5.2, -4.4) * mm, "mid": v(-5.36, -4.44) * mm, "end": v(-5.48, -4.36) * mm});
            skLineSegment(sketch, "E59.8.5", {"start": v(-4.4, -5.2) * mm, "end": v(-3.94, -4.54) * mm});
            skArc(sketch, "E59.8.6", {"start": v(-4.4, -5.2) * mm, "mid": v(-4.44, -5.36) * mm, "end": v(-4.36, -5.48) * mm});
            skLineSegment(sketch, "E59.8.7", {"start": v(-4.11, -5.66) * mm, "end": v(-4.36, -5.48) * mm});
            skLineSegment(sketch, "E59.9.0", {"start": v(-4.11, -5.66) * mm, "end": v(-3.87, -5.84) * mm});
            skLineSegment(sketch, "E59.9.1", {"start": v(-2.35, -5.54) * mm, "end": v(-2.72, -5.35) * mm});
            skLineSegment(sketch, "E59.9.2", {"start": v(-3.6, -5.8) * mm, "end": v(-3.1, -5.15) * mm});
            skLineSegment(sketch, "E59.9.3", {"start": v(-3.1, -5.15) * mm, "end": v(-2.72, -5.35) * mm});
            skArc(sketch, "E59.9.4", {"start": v(-3.6, -5.8) * mm, "mid": v(-3.72, -5.88) * mm, "end": v(-3.87, -5.84) * mm});
            skLineSegment(sketch, "E59.9.5", {"start": v(-2.58, -6.32) * mm, "end": v(-2.35, -5.54) * mm});
            skArc(sketch, "E59.9.6", {"start": v(-2.58, -6.32) * mm, "mid": v(-2.57, -6.47) * mm, "end": v(-2.45, -6.56) * mm});
            skLineSegment(sketch, "E59.9.7", {"start": v(-2.16, -6.66) * mm, "end": v(-2.45, -6.56) * mm});
            skLineSegment(sketch, "E59.10.0", {"start": v(-2.16, -6.66) * mm, "end": v(-1.87, -6.75) * mm});
            skLineSegment(sketch, "E59.10.1", {"start": v(-0.52, -6) * mm, "end": v(-0.94, -5.93) * mm});
            skLineSegment(sketch, "E59.10.2", {"start": v(-1.62, -6.63) * mm, "end": v(-1.36, -5.86) * mm});
            skLineSegment(sketch, "E59.10.3", {"start": v(-1.36, -5.86) * mm, "end": v(-0.94, -5.93) * mm});
            skArc(sketch, "E59.10.4", {"start": v(-1.62, -6.63) * mm, "mid": v(-1.72, -6.74) * mm, "end": v(-1.87, -6.75) * mm});
            skLineSegment(sketch, "E59.10.5", {"start": v(-0.5, -6.8) * mm, "end": v(-0.52, -6) * mm});
            skArc(sketch, "E59.10.6", {"start": v(-0.5, -6.8) * mm, "mid": v(-0.44, -6.94) * mm, "end": v(-0.3, -7) * mm});
            skLineSegment(sketch, "E59.10.7", {"start": v(0, -7) * mm, "end": v(-0.3, -7) * mm});
            skLineSegment(sketch, "E59.11.0", {"start": v(0, -7) * mm, "end": v(0.3, -7) * mm});
            skLineSegment(sketch, "E59.11.1", {"start": v(1.36, -5.86) * mm, "end": v(0.94, -5.93) * mm});
            skLineSegment(sketch, "E59.11.2", {"start": v(0.5, -6.8) * mm, "end": v(0.52, -6) * mm});
            skLineSegment(sketch, "E59.11.3", {"start": v(0.52, -6) * mm, "end": v(0.94, -5.93) * mm});
            skArc(sketch, "E59.11.4", {"start": v(0.5, -6.8) * mm, "mid": v(0.44, -6.94) * mm, "end": v(0.3, -7) * mm});
            skLineSegment(sketch, "E59.11.5", {"start": v(1.62, -6.63) * mm, "end": v(1.36, -5.86) * mm});
            skArc(sketch, "E59.11.6", {"start": v(1.62, -6.63) * mm, "mid": v(1.72, -6.74) * mm, "end": v(1.87, -6.75) * mm});
            skLineSegment(sketch, "E59.11.7", {"start": v(2.16, -6.66) * mm, "end": v(1.87, -6.75) * mm});
            skLineSegment(sketch, "E59.12.0", {"start": v(2.16, -6.66) * mm, "end": v(2.45, -6.56) * mm});
            skLineSegment(sketch, "E59.12.1", {"start": v(3.1, -5.15) * mm, "end": v(2.72, -5.35) * mm});
            skLineSegment(sketch, "E59.12.2", {"start": v(2.58, -6.32) * mm, "end": v(2.35, -5.54) * mm});
            skLineSegment(sketch, "E59.12.3", {"start": v(2.35, -5.54) * mm, "end": v(2.72, -5.35) * mm});
            skArc(sketch, "E59.12.4", {"start": v(2.58, -6.32) * mm, "mid": v(2.57, -6.47) * mm, "end": v(2.45, -6.56) * mm});
            skLineSegment(sketch, "E59.12.5", {"start": v(3.6, -5.8) * mm, "end": v(3.1, -5.15) * mm});
            skArc(sketch, "E59.12.6", {"start": v(3.6, -5.8) * mm, "mid": v(3.72, -5.88) * mm, "end": v(3.87, -5.84) * mm});
            skLineSegment(sketch, "E59.12.7", {"start": v(4.11, -5.66) * mm, "end": v(3.87, -5.84) * mm});
            skLineSegment(sketch, "E59.13.0", {"start": v(4.11, -5.66) * mm, "end": v(4.36, -5.48) * mm});
            skLineSegment(sketch, "E59.13.1", {"start": v(4.54, -3.94) * mm, "end": v(4.24, -4.24) * mm});
            skLineSegment(sketch, "E59.13.2", {"start": v(4.4, -5.2) * mm, "end": v(3.94, -4.54) * mm});
            skLineSegment(sketch, "E59.13.3", {"start": v(3.94, -4.54) * mm, "end": v(4.24, -4.24) * mm});
            skArc(sketch, "E59.13.4", {"start": v(4.4, -5.2) * mm, "mid": v(4.44, -5.36) * mm, "end": v(4.36, -5.48) * mm});
            skLineSegment(sketch, "E59.13.5", {"start": v(5.2, -4.4) * mm, "end": v(4.54, -3.94) * mm});
            skArc(sketch, "E59.13.6", {"start": v(5.2, -4.4) * mm, "mid": v(5.36, -4.44) * mm, "end": v(5.48, -4.36) * mm});
            skLineSegment(sketch, "E59.13.7", {"start": v(5.66, -4.11) * mm, "end": v(5.48, -4.36) * mm});
            skLineSegment(sketch, "E59.14.0", {"start": v(5.66, -4.11) * mm, "end": v(5.84, -3.87) * mm});
            skLineSegment(sketch, "E59.14.1", {"start": v(5.54, -2.35) * mm, "end": v(5.35, -2.72) * mm});
            skLineSegment(sketch, "E59.14.2", {"start": v(5.8, -3.6) * mm, "end": v(5.15, -3.1) * mm});
            skLineSegment(sketch, "E59.14.3", {"start": v(5.15, -3.1) * mm, "end": v(5.35, -2.72) * mm});
            skArc(sketch, "E59.14.4", {"start": v(5.8, -3.6) * mm, "mid": v(5.88, -3.72) * mm, "end": v(5.84, -3.87) * mm});
            skLineSegment(sketch, "E59.14.5", {"start": v(6.32, -2.58) * mm, "end": v(5.54, -2.35) * mm});
            skArc(sketch, "E59.14.6", {"start": v(6.32, -2.58) * mm, "mid": v(6.47, -2.57) * mm, "end": v(6.56, -2.45) * mm});
            skLineSegment(sketch, "E59.14.7", {"start": v(6.66, -2.16) * mm, "end": v(6.56, -2.45) * mm});
            skLineSegment(sketch, "E59.15.0", {"start": v(6.66, -2.16) * mm, "end": v(6.75, -1.87) * mm});
            skLineSegment(sketch, "E59.15.1", {"start": v(6, -0.52) * mm, "end": v(5.93, -0.94) * mm});
            skLineSegment(sketch, "E59.15.2", {"start": v(6.63, -1.62) * mm, "end": v(5.86, -1.36) * mm});
            skLineSegment(sketch, "E59.15.3", {"start": v(5.86, -1.36) * mm, "end": v(5.93, -0.94) * mm});
            skArc(sketch, "E59.15.4", {"start": v(6.63, -1.62) * mm, "mid": v(6.74, -1.72) * mm, "end": v(6.75, -1.87) * mm});
            skLineSegment(sketch, "E59.15.5", {"start": v(6.8, -0.5) * mm, "end": v(6, -0.52) * mm});
            skArc(sketch, "E59.15.6", {"start": v(6.8, -0.5) * mm, "mid": v(6.94, -0.44) * mm, "end": v(7, -0.3) * mm});
            skLineSegment(sketch, "E59.15.7", {"start": v(7, 0) * mm, "end": v(7, -0.3) * mm});
            skLineSegment(sketch, "E59.16.0", {"start": v(7, 0) * mm, "end": v(7, 0.3) * mm});
            skLineSegment(sketch, "E59.16.1", {"start": v(5.86, 1.36) * mm, "end": v(5.93, 0.94) * mm});
            skLineSegment(sketch, "E59.16.2", {"start": v(6.8, 0.5) * mm, "end": v(6, 0.52) * mm});
            skLineSegment(sketch, "E59.16.3", {"start": v(6, 0.52) * mm, "end": v(5.93, 0.94) * mm});
            skArc(sketch, "E59.16.4", {"start": v(6.8, 0.5) * mm, "mid": v(6.94, 0.44) * mm, "end": v(7, 0.3) * mm});
            skLineSegment(sketch, "E59.16.5", {"start": v(6.63, 1.62) * mm, "end": v(5.86, 1.36) * mm});
            skArc(sketch, "E59.16.6", {"start": v(6.63, 1.62) * mm, "mid": v(6.74, 1.72) * mm, "end": v(6.75, 1.87) * mm});
            skLineSegment(sketch, "E59.16.7", {"start": v(6.66, 2.16) * mm, "end": v(6.75, 1.87) * mm});
            skLineSegment(sketch, "E59.17.0", {"start": v(6.66, 2.16) * mm, "end": v(6.56, 2.45) * mm});
            skLineSegment(sketch, "E59.17.1", {"start": v(5.15, 3.1) * mm, "end": v(5.35, 2.72) * mm});
            skLineSegment(sketch, "E59.17.2", {"start": v(6.32, 2.58) * mm, "end": v(5.54, 2.35) * mm});
            skLineSegment(sketch, "E59.17.3", {"start": v(5.54, 2.35) * mm, "end": v(5.35, 2.72) * mm});
            skArc(sketch, "E59.17.4", {"start": v(6.32, 2.58) * mm, "mid": v(6.47, 2.57) * mm, "end": v(6.56, 2.45) * mm});
            skLineSegment(sketch, "E59.17.5", {"start": v(5.8, 3.6) * mm, "end": v(5.15, 3.1) * mm});
            skArc(sketch, "E59.17.6", {"start": v(5.8, 3.6) * mm, "mid": v(5.88, 3.72) * mm, "end": v(5.84, 3.87) * mm});
            skLineSegment(sketch, "E59.17.7", {"start": v(5.66, 4.11) * mm, "end": v(5.84, 3.87) * mm});
            skLineSegment(sketch, "E59.18.0", {"start": v(5.66, 4.11) * mm, "end": v(5.48, 4.36) * mm});
            skLineSegment(sketch, "E59.18.1", {"start": v(3.94, 4.54) * mm, "end": v(4.24, 4.24) * mm});
            skLineSegment(sketch, "E59.18.2", {"start": v(5.2, 4.4) * mm, "end": v(4.54, 3.94) * mm});
            skLineSegment(sketch, "E59.18.3", {"start": v(4.54, 3.94) * mm, "end": v(4.24, 4.24) * mm});
            skArc(sketch, "E59.18.4", {"start": v(5.2, 4.4) * mm, "mid": v(5.36, 4.44) * mm, "end": v(5.48, 4.36) * mm});
            skLineSegment(sketch, "E59.18.5", {"start": v(4.4, 5.2) * mm, "end": v(3.94, 4.54) * mm});
            skArc(sketch, "E59.18.6", {"start": v(4.4, 5.2) * mm, "mid": v(4.44, 5.36) * mm, "end": v(4.36, 5.48) * mm});
            skLineSegment(sketch, "E59.18.7", {"start": v(4.11, 5.66) * mm, "end": v(4.36, 5.48) * mm});
            skLineSegment(sketch, "E59.19.0", {"start": v(4.11, 5.66) * mm, "end": v(3.87, 5.84) * mm});
            skLineSegment(sketch, "E59.19.1", {"start": v(2.35, 5.54) * mm, "end": v(2.72, 5.35) * mm});
            skLineSegment(sketch, "E59.19.2", {"start": v(3.6, 5.8) * mm, "end": v(3.1, 5.15) * mm});
            skLineSegment(sketch, "E59.19.3", {"start": v(3.1, 5.15) * mm, "end": v(2.72, 5.35) * mm});
            skArc(sketch, "E59.19.4", {"start": v(3.6, 5.8) * mm, "mid": v(3.72, 5.88) * mm, "end": v(3.87, 5.84) * mm});
            skLineSegment(sketch, "E59.19.5", {"start": v(2.58, 6.32) * mm, "end": v(2.35, 5.54) * mm});
            skArc(sketch, "E59.19.6", {"start": v(2.58, 6.32) * mm, "mid": v(2.57, 6.47) * mm, "end": v(2.45, 6.56) * mm});
            skLineSegment(sketch, "E59.19.7", {"start": v(2.16, 6.66) * mm, "end": v(2.45, 6.56) * mm});
            skPoint(sketch, "E59.center", {"position": v(0, 0) * mm});
            skSolve(sketch);
        }
        {
            var Q0;
            Q0=qSketchRegion(id+"F35",true);
            extrude(context, id + "F36", {"entities" : qUnion([Q0]), "depth" : 3 * mm});
        }
        {
            var Q0;
            Q0=makeQuery(id+"F36.opExtrude","CAP_FACE",FACE,{"disambiguationData":[OSD([sQuery(id+"F35.wireOp",EDGE,"E51"),sQuery(id+"F35.wireOp",EDGE,"E52"),sQuery(id+"F35.wireOp",EDGE,"E53"),sQuery(id+"F35.wireOp",EDGE,"E54.filletArc"),sQuery(id+"F35.wireOp",EDGE,"E55.MirrorCS"),sQuery(id+"F35.wireOp",EDGE,"E56.MirrorCS"),sQuery(id+"F35.wireOp",EDGE,"E57.MirrorCS"),sQuery(id+"F35.wireOp",EDGE,"E58.MirrorCS"),sQuery(id+"F35.wireOp",EDGE,"E59.1.0"),sQuery(id+"F35.wireOp",EDGE,"E59.1.1"),sQuery(id+"F35.wireOp",EDGE,"E59.1.2"),sQuery(id+"F35.wireOp",EDGE,"E59.1.3"),sQuery(id+"F35.wireOp",EDGE,"E59.1.4"),sQuery(id+"F35.wireOp",EDGE,"E59.1.5"),sQuery(id+"F35.wireOp",EDGE,"E59.1.6"),sQuery(id+"F35.wireOp",EDGE,"E59.1.7"),sQuery(id+"F35.wireOp",EDGE,"E59.2.0"),sQuery(id+"F35.wireOp",EDGE,"E59.2.1"),sQuery(id+"F35.wireOp",EDGE,"E59.2.2"),sQuery(id+"F35.wireOp",EDGE,"E59.2.3"),sQuery(id+"F35.wireOp",EDGE,"E59.2.4"),sQuery(id+"F35.wireOp",EDGE,"E59.2.5"),sQuery(id+"F35.wireOp",EDGE,"E59.2.6"),sQuery(id+"F35.wireOp",EDGE,"E59.2.7"),sQuery(id+"F35.wireOp",EDGE,"E59.3.0"),sQuery(id+"F35.wireOp",EDGE,"E59.3.1"),sQuery(id+"F35.wireOp",EDGE,"E59.3.2"),sQuery(id+"F35.wireOp",EDGE,"E59.3.3"),sQuery(id+"F35.wireOp",EDGE,"E59.3.4"),sQuery(id+"F35.wireOp",EDGE,"E59.3.5"),sQuery(id+"F35.wireOp",EDGE,"E59.3.6"),sQuery(id+"F35.wireOp",EDGE,"E59.3.7"),sQuery(id+"F35.wireOp",EDGE,"E59.4.0"),sQuery(id+"F35.wireOp",EDGE,"E59.4.1"),sQuery(id+"F35.wireOp",EDGE,"E59.4.2"),sQuery(id+"F35.wireOp",EDGE,"E59.4.3"),sQuery(id+"F35.wireOp",EDGE,"E59.4.4"),sQuery(id+"F35.wireOp",EDGE,"E59.4.5"),sQuery(id+"F35.wireOp",EDGE,"E59.4.6"),sQuery(id+"F35.wireOp",EDGE,"E59.4.7"),sQuery(id+"F35.wireOp",EDGE,"E59.5.0"),sQuery(id+"F35.wireOp",EDGE,"E59.5.1"),sQuery(id+"F35.wireOp",EDGE,"E59.5.2"),sQuery(id+"F35.wireOp",EDGE,"E59.5.3"),sQuery(id+"F35.wireOp",EDGE,"E59.5.4"),sQuery(id+"F35.wireOp",EDGE,"E59.5.5"),sQuery(id+"F35.wireOp",EDGE,"E59.5.6"),sQuery(id+"F35.wireOp",EDGE,"E59.5.7"),sQuery(id+"F35.wireOp",EDGE,"E59.6.0"),sQuery(id+"F35.wireOp",EDGE,"E59.6.1"),sQuery(id+"F35.wireOp",EDGE,"E59.6.2"),sQuery(id+"F35.wireOp",EDGE,"E59.6.3"),sQuery(id+"F35.wireOp",EDGE,"E59.6.4"),sQuery(id+"F35.wireOp",EDGE,"E59.6.5"),sQuery(id+"F35.wireOp",EDGE,"E59.6.6"),sQuery(id+"F35.wireOp",EDGE,"E59.6.7"),sQuery(id+"F35.wireOp",EDGE,"E59.7.0"),sQuery(id+"F35.wireOp",EDGE,"E59.7.1"),sQuery(id+"F35.wireOp",EDGE,"E59.7.2"),sQuery(id+"F35.wireOp",EDGE,"E59.7.3"),sQuery(id+"F35.wireOp",EDGE,"E59.7.4"),sQuery(id+"F35.wireOp",EDGE,"E59.7.5"),sQuery(id+"F35.wireOp",EDGE,"E59.7.6"),sQuery(id+"F35.wireOp",EDGE,"E59.7.7"),sQuery(id+"F35.wireOp",EDGE,"E59.8.0"),sQuery(id+"F35.wireOp",EDGE,"E59.8.1"),sQuery(id+"F35.wireOp",EDGE,"E59.8.2"),sQuery(id+"F35.wireOp",EDGE,"E59.8.3"),sQuery(id+"F35.wireOp",EDGE,"E59.8.4"),sQuery(id+"F35.wireOp",EDGE,"E59.8.5"),sQuery(id+"F35.wireOp",EDGE,"E59.8.6"),sQuery(id+"F35.wireOp",EDGE,"E59.8.7"),sQuery(id+"F35.wireOp",EDGE,"E59.9.0"),sQuery(id+"F35.wireOp",EDGE,"E59.9.1"),sQuery(id+"F35.wireOp",EDGE,"E59.9.2"),sQuery(id+"F35.wireOp",EDGE,"E59.9.3"),sQuery(id+"F35.wireOp",EDGE,"E59.9.4"),sQuery(id+"F35.wireOp",EDGE,"E59.9.5"),sQuery(id+"F35.wireOp",EDGE,"E59.9.6"),sQuery(id+"F35.wireOp",EDGE,"E59.9.7"),sQuery(id+"F35.wireOp",EDGE,"E59.10.0"),sQuery(id+"F35.wireOp",EDGE,"E59.10.1"),sQuery(id+"F35.wireOp",EDGE,"E59.10.2"),sQuery(id+"F35.wireOp",EDGE,"E59.10.3"),sQuery(id+"F35.wireOp",EDGE,"E59.10.4"),sQuery(id+"F35.wireOp",EDGE,"E59.10.5"),sQuery(id+"F35.wireOp",EDGE,"E59.10.6"),sQuery(id+"F35.wireOp",EDGE,"E59.10.7"),sQuery(id+"F35.wireOp",EDGE,"E59.11.0"),sQuery(id+"F35.wireOp",EDGE,"E59.11.1"),sQuery(id+"F35.wireOp",EDGE,"E59.11.2"),sQuery(id+"F35.wireOp",EDGE,"E59.11.3"),sQuery(id+"F35.wireOp",EDGE,"E59.11.4"),sQuery(id+"F35.wireOp",EDGE,"E59.11.5"),sQuery(id+"F35.wireOp",EDGE,"E59.11.6"),sQuery(id+"F35.wireOp",EDGE,"E59.11.7"),sQuery(id+"F35.wireOp",EDGE,"E59.12.0"),sQuery(id+"F35.wireOp",EDGE,"E59.12.1"),sQuery(id+"F35.wireOp",EDGE,"E59.12.2"),sQuery(id+"F35.wireOp",EDGE,"E59.12.3"),sQuery(id+"F35.wireOp",EDGE,"E59.12.4"),sQuery(id+"F35.wireOp",EDGE,"E59.12.5"),sQuery(id+"F35.wireOp",EDGE,"E59.12.6"),sQuery(id+"F35.wireOp",EDGE,"E59.12.7"),sQuery(id+"F35.wireOp",EDGE,"E59.13.0"),sQuery(id+"F35.wireOp",EDGE,"E59.13.1"),sQuery(id+"F35.wireOp",EDGE,"E59.13.2"),sQuery(id+"F35.wireOp",EDGE,"E59.13.3"),sQuery(id+"F35.wireOp",EDGE,"E59.13.4"),sQuery(id+"F35.wireOp",EDGE,"E59.13.5"),sQuery(id+"F35.wireOp",EDGE,"E59.13.6"),sQuery(id+"F35.wireOp",EDGE,"E59.13.7"),sQuery(id+"F35.wireOp",EDGE,"E59.14.0"),sQuery(id+"F35.wireOp",EDGE,"E59.14.1"),sQuery(id+"F35.wireOp",EDGE,"E59.14.2"),sQuery(id+"F35.wireOp",EDGE,"E59.14.3"),sQuery(id+"F35.wireOp",EDGE,"E59.14.4"),sQuery(id+"F35.wireOp",EDGE,"E59.14.5"),sQuery(id+"F35.wireOp",EDGE,"E59.14.6"),sQuery(id+"F35.wireOp",EDGE,"E59.14.7"),sQuery(id+"F35.wireOp",EDGE,"E59.15.0"),sQuery(id+"F35.wireOp",EDGE,"E59.15.1"),sQuery(id+"F35.wireOp",EDGE,"E59.15.2"),sQuery(id+"F35.wireOp",EDGE,"E59.15.3"),sQuery(id+"F35.wireOp",EDGE,"E59.15.4"),sQuery(id+"F35.wireOp",EDGE,"E59.15.5"),sQuery(id+"F35.wireOp",EDGE,"E59.15.6"),sQuery(id+"F35.wireOp",EDGE,"E59.15.7"),sQuery(id+"F35.wireOp",EDGE,"E59.16.0"),sQuery(id+"F35.wireOp",EDGE,"E59.16.1"),sQuery(id+"F35.wireOp",EDGE,"E59.16.2"),sQuery(id+"F35.wireOp",EDGE,"E59.16.3"),sQuery(id+"F35.wireOp",EDGE,"E59.16.4"),sQuery(id+"F35.wireOp",EDGE,"E59.16.5"),sQuery(id+"F35.wireOp",EDGE,"E59.16.6"),sQuery(id+"F35.wireOp",EDGE,"E59.16.7"),sQuery(id+"F35.wireOp",EDGE,"E59.17.0"),sQuery(id+"F35.wireOp",EDGE,"E59.17.1"),sQuery(id+"F35.wireOp",EDGE,"E59.17.2"),sQuery(id+"F35.wireOp",EDGE,"E59.17.3"),sQuery(id+"F35.wireOp",EDGE,"E59.17.4"),sQuery(id+"F35.wireOp",EDGE,"E59.17.5"),sQuery(id+"F35.wireOp",EDGE,"E59.17.6"),sQuery(id+"F35.wireOp",EDGE,"E59.17.7"),sQuery(id+"F35.wireOp",EDGE,"E59.18.0"),sQuery(id+"F35.wireOp",EDGE,"E59.18.1"),sQuery(id+"F35.wireOp",EDGE,"E59.18.2"),sQuery(id+"F35.wireOp",EDGE,"E59.18.3"),sQuery(id+"F35.wireOp",EDGE,"E59.18.4"),sQuery(id+"F35.wireOp",EDGE,"E59.18.5"),sQuery(id+"F35.wireOp",EDGE,"E59.18.6"),sQuery(id+"F35.wireOp",EDGE,"E59.18.7"),sQuery(id+"F35.wireOp",EDGE,"E59.19.0"),sQuery(id+"F35.wireOp",EDGE,"E59.19.1"),sQuery(id+"F35.wireOp",EDGE,"E59.19.2"),sQuery(id+"F35.wireOp",EDGE,"E59.19.3"),sQuery(id+"F35.wireOp",EDGE,"E59.19.4"),sQuery(id+"F35.wireOp",EDGE,"E59.19.5"),sQuery(id+"F35.wireOp",EDGE,"E59.19.6"),sQuery(id+"F35.wireOp",EDGE,"E59.19.7")])],"isStart":false});
            var sketch = newSketch(context, id + "F37", { "sketchPlane" : qUnion([Q0])});
            skCircle(sketch, "E60", {"center": v(0, 0) * mm, "radius": 4.8 * mm});
            skSolve(sketch);
        }
        {
            var Q0;
            Q0=qSketchRegion(id+"F37",true);
            extrude(context, id + "F38", {"entities" : qUnion([Q0]), "operationType" : NewBodyOperationType.REMOVE, "oppositeDirection" : true, "depth" : 25 * mm});
        }
        {
            var Q0;
            Q0=qCreatedBy(makeId("Top.planeOp"),FACE);
            var sketch = newSketch(context, id + "F39", { "sketchPlane" : qUnion([Q0])});
            skCircle(sketch, "E61", {"center": v(10.5, 0) * mm, "radius": 1 * mm});
            skCircle(sketch, "E62", {"center": v(-5.25, 9.1) * mm, "radius": 1 * mm});
            skCircle(sketch, "E63", {"center": v(-5.25, -9.1) * mm, "radius": 1 * mm});
            skSolve(sketch);
        }
        {
            var Q0;
            Q0=qSketchRegion(id+"F39",true);
            extrude(context, id + "F40", {"entities" : qUnion([Q0]), "operationType" : NewBodyOperationType.REMOVE, "oppositeDirection" : true, "depth" : 25 * mm});
        }
    });
